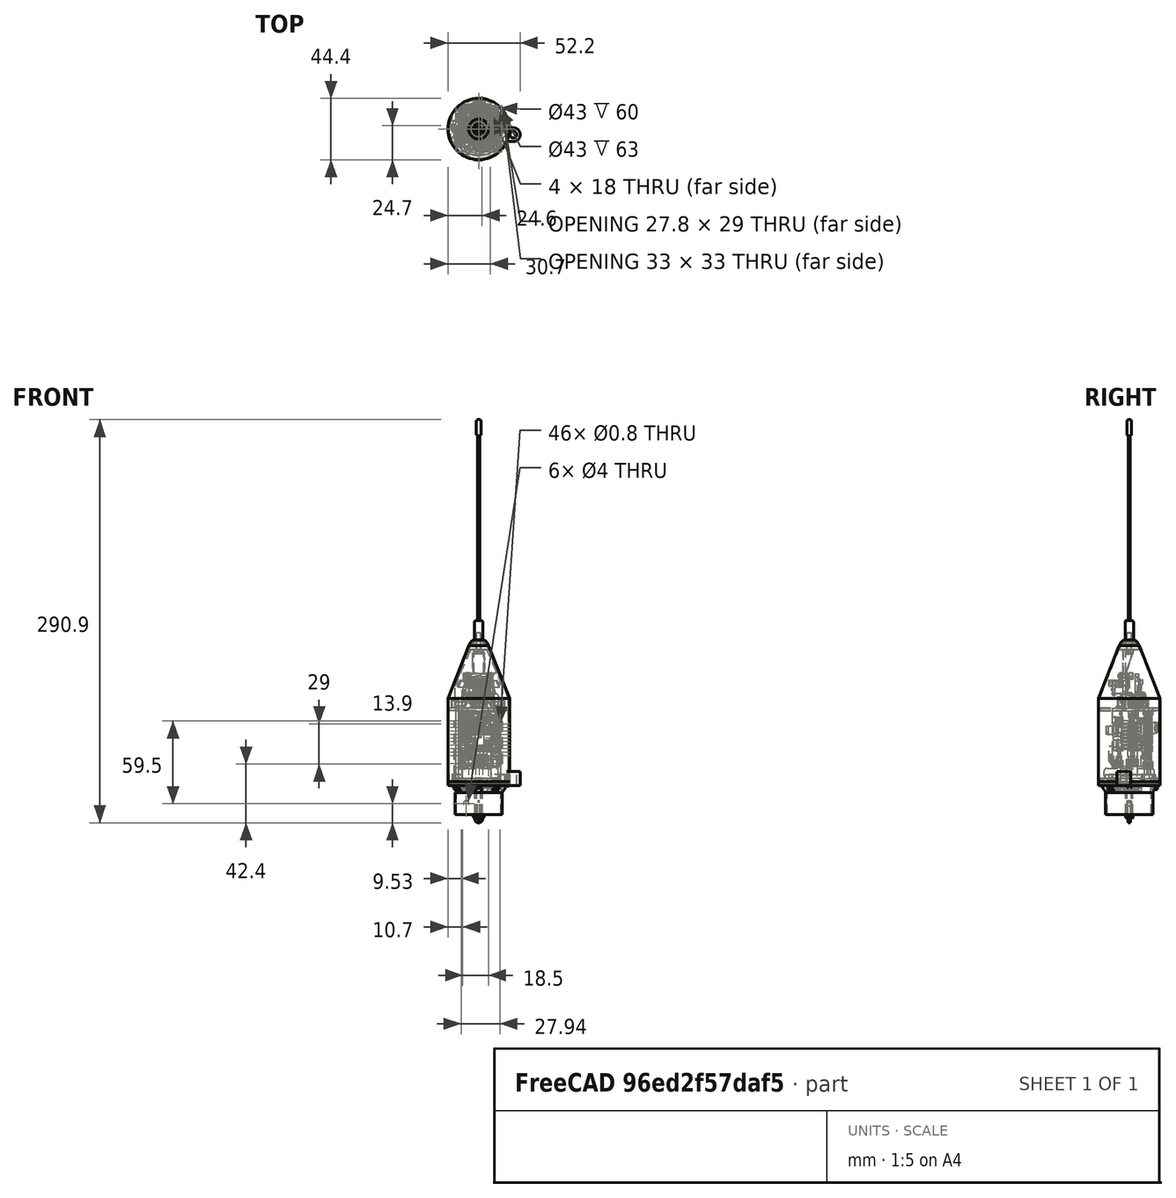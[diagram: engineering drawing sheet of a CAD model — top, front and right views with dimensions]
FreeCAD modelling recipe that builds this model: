
FCSTD DOCUMENT  (FreeCAD 0.18R4 (GitTag))
Label: fli3d structure v4.2
License: All rights reserved
LicenseURL: http://en.wikipedia.org/wiki/All_rights_reserved
objects: Part::Feature×223, Part::Cylinder×216, Part::Box×145, Part::Cut×97, Part::Compound×93, Part::Chamfer×44, Part::MultiFuse×30, Part::Prism×23, Part::Cone×9, Part::Fillet×7, Part::MultiCommon×7, Mesh::Feature×4, Part::Sphere×2, Part::Torus×1, App::Part×1
note: 897 computed .brp shape members not serialized (recipe doc carries the construction recipe); baked Part::Feature solids carry a one-line shape summary decoded from their .brp

FEATURE [Part::Cylinder] Cylinder
  Angle = 360
  AttacherType = Attacher::AttachEngine3D
  Height = 16
  Radius = 17
FEATURE [Part::Cylinder] Cylinder001  label="cut-out screw"
  Angle = 360
  AttacherType = Attacher::AttachEngine3D
  Height = 10
  Placement = pos=(0,0,1) rot=(0,0,1;0rad)
  Radius = 0.9
FEATURE [Part::Cylinder] Cylinder002
  Angle = 360
  AttacherType = Attacher::AttachEngine3D
  Height = 10
  Placement = pos=(0,0,-1) rot=(0,0,1;0rad)
  Radius = 0.9
FEATURE [Part::Torus] Torus
  Angle1 = -180
  Angle2 = 180
  Angle3 = 360
  AttacherType = Attacher::AttachEngine3D
  Placement = pos=(0,0,-3) rot=(1,0,0;1.5708rad)
  Radius1 = 2
  Radius2 = 0.9
FEATURE [Part::Compound] Compound  label="Eye screw"
  Links = -> [Torus,Cylinder002]
  Placement = pos=(0,0,1) rot=(0,0,1;0rad)
FEATURE [Part::Cylinder] Cylinder003
  Angle = 360
  AttacherType = Attacher::AttachEngine3D
  Height = 60
  Radius = 22.2
FEATURE [Part::Cylinder] Cylinder004
  Angle = 360
  AttacherType = Attacher::AttachEngine3D
  Height = 60
  Radius = 21.5
FEATURE [Part::Cut] Cut002
  Base = -> Cylinder003
  Placement = pos=(0,0,25) rot=(0,0,1;0rad)
  Tool = -> Cylinder004
FEATURE [Part::Cone] Cone001  label="Cone004"
  Angle = 360
  AttacherType = Attacher::AttachEngine3D
  Height = 41
  Placement = pos=(0,0,75) rot=(0,0,1;0rad)
  Radius1 = 22.2
  Radius2 = 6
FEATURE [Part::Cone] Cone002  label="Cone001"
  Angle = 360
  AttacherType = Attacher::AttachEngine3D
  Height = 41
  Placement = pos=(0,0,75) rot=(0,0,1;0rad)
  Radius1 = 21.5
  Radius2 = 5.3
FEATURE [Part::Cut] Cut003  label="compound"
  Base = -> Cone001
  Placement = pos=(0,0,10) rot=(0,0,1;0rad)
  Tool = -> Cone002
FEATURE [Part::Cylinder] Cylinder005
  Angle = 360
  AttacherType = Attacher::AttachEngine3D
  Height = 10
  Placement = pos=(0.5,26,66) rot=(1,0,0;1.5708rad)
  Radius = 2.75
FEATURE [Part::Cut] Cut004  label="cylindrical section"
  Base = -> Cut002
  Tool = -> Cylinder005
FEATURE [Part::Cylinder] Cylinder006
  Angle = 360
  AttacherType = Attacher::AttachEngine3D
  Height = 14
  Placement = pos=(0,0,150) rot=(0,0,1;0rad)
  Radius = 3
FEATURE [Part::Cylinder] Cylinder007
  Angle = 360
  AttacherType = Attacher::AttachEngine3D
  Height = 133
  Placement = pos=(0,0,164) rot=(0,0,1;0rad)
  Radius = 0.75
FEATURE [Part::Cylinder] Cylinder008
  Angle = 360
  AttacherType = Attacher::AttachEngine3D
  Height = 11.5
  Placement = pos=(0,0,297.5) rot=(0,0,1;0rad)
  Radius = 1.65
FEATURE [Part::Cylinder] Cylinder009
  Angle = 360
  AttacherType = Attacher::AttachEngine3D
  Height = 5
  Placement = pos=(0,0,150) rot=(0,0,1;0rad)
  Radius = 1.5
FEATURE [Part::Fillet] Fillet
  Base = -> Cylinder006
  Edges = 1 edges r=1: [Edge1]
FEATURE [Part::Cut] Cut005
  Base = -> Fillet
  Tool = -> Cylinder009
FEATURE [Part::Fillet] Fillet001
  Base = -> Cylinder008
  Edges = 2 edges r=1: [Edge1,Edge3]
FEATURE [Part::Compound] Compound003  label="433 MHz antenna"
  Links = -> [Cylinder007,Cut005,Fillet001]
  Placement = pos=(0,0,-23) rot=(0,0,1;0rad)
FEATURE [Part::Cylinder] Cylinder010
  Angle = 360
  AttacherType = Attacher::AttachEngine3D
  Height = 10
  Placement = pos=(0,0,118) rot=(0,0,1;0rad)
  Radius = 1.7
FEATURE [Part::Cylinder] Cylinder012
  Angle = 360
  AttacherType = Attacher::AttachEngine3D
  Height = 12
  Placement = pos=(0,0,-20) rot=(0,0,1;0rad)
  Radius = 1.5
FEATURE [Part::Cylinder] Cylinder013
  Angle = 360
  AttacherType = Attacher::AttachEngine3D
  Height = 3
  Placement = pos=(0,0,-23) rot=(0,0,1;0rad)
  Radius = 2.7
FEATURE [Part::Prism] Prism
  AttacherType = Attacher::AttachEngine3D
  Circumradius = 1.4
  Height = 2
  Placement = pos=(0,0,-23) rot=(0,0,1;0rad)
  Polygon = 6
FEATURE [Part::Cut] Cut008
  Base = -> Cylinder013
  Tool = -> Prism
FEATURE [Part::Compound] Compound005  label="M3x12 hex"
  Links = -> [Cylinder012,Cut008]
  Placement = pos=(0,0,140) rot=(0,0,1;0rad)
FEATURE [Part::Cylinder] Cylinder031
  Angle = 360
  AttacherType = Attacher::AttachEngine3D
  Height = 8
  Placement = pos=(0,0,-20) rot=(0,0,1;0rad)
  Radius = 1.25
FEATURE [Part::Cylinder] Cylinder032
  Angle = 360
  AttacherType = Attacher::AttachEngine3D
  Height = 2.5
  Placement = pos=(0,0,-22.5) rot=(0,0,1;0rad)
  Radius = 2.34
FEATURE [Part::Prism] Prism004
  AttacherType = Attacher::AttachEngine3D
  Circumradius = 1
  Height = 1.1
  Placement = pos=(0,0,-23) rot=(0,0,1;0rad)
  Polygon = 6
FEATURE [Part::Cut] Cut024
  Base = -> Cylinder032
  Tool = -> Prism004
FEATURE [Part::Compound] Compound013  label="M2.5x8 hex003"
  Links = -> [Cylinder031,Cut024]
  Placement = pos=(3,1,81) rot=(0,1,0;1.5708rad)
FEATURE [Part::Cylinder] Cylinder033
  Angle = 360
  AttacherType = Attacher::AttachEngine3D
  Height = 8
  Placement = pos=(0,0,-20) rot=(0,0,1;0rad)
  Radius = 1.25
FEATURE [Part::Cylinder] Cylinder034
  Angle = 360
  AttacherType = Attacher::AttachEngine3D
  Height = 2.5
  Placement = pos=(0,0,-22.5) rot=(0,0,1;0rad)
  Radius = 2.34
FEATURE [Part::Prism] Prism005
  AttacherType = Attacher::AttachEngine3D
  Circumradius = 1
  Height = 1.1
  Placement = pos=(0,0,-23) rot=(0,0,1;0rad)
  Polygon = 6
FEATURE [Part::Cut] Cut025
  Base = -> Cylinder034
  Tool = -> Prism005
FEATURE [Part::Compound] Compound014  label="M2.5x8 hex004"
  Links = -> [Cylinder033,Cut025]
  Placement = pos=(-4,8,81) rot=(0,-1,0;1.5708rad)
FEATURE [Part::Feature] Part__Feature183  label="pcb"
  shape: bbox 20.5 x 16 x 1.5 mm, 92 faces (baked)
FEATURE [Part::Feature] Part__Feature184  label="pcb001"
  shape: bbox 5.2 x 4.498 x 1 mm, 6 faces (baked)
FEATURE [Part::Feature] Part__Feature185  label="pcb002"
  shape: bbox 4.542 x 2.102 x 1.5 mm, 6 faces (baked)
FEATURE [Part::Feature] Part__Feature186  label="pcb003"
  shape: bbox 1.036 x 2.536 x 1 mm, 6 faces (baked)
FEATURE [Part::Feature] Part__Feature187  label="pcb004"
  shape: bbox 0.9209 x 2 x 1 mm, 6 faces (baked)
FEATURE [Part::Feature] Part__Feature188  label="pcb005"
  shape: bbox 1 x 2 x 1 mm, 6 faces (baked)
FEATURE [Part::Feature] Part__Feature189  label="pcb006"
  shape: bbox 1.036 x 2.536 x 1 mm, 6 faces (baked)
FEATURE [Part::Feature] Part__Feature190  label="pcb007"
  shape: bbox 1 x 2 x 1 mm, 6 faces (baked)
FEATURE [Part::Feature] Part__Feature191  label="pcb008"
  shape: bbox 2 x 1 x 1 mm, 6 faces (baked)
FEATURE [Part::Feature] Part__Feature192  label="pcb009"
  shape: bbox 1.036 x 2.536 x 1 mm, 6 faces (baked)
FEATURE [Part::Feature] Part__Feature193  label="pcb010"
  shape: bbox 1.036 x 2.536 x 1 mm, 6 faces (baked)
FEATURE [Part::Feature] Part__Feature194  label="pcb011"
  shape: bbox 0.9209 x 2 x 1 mm, 6 faces (baked)
FEATURE [Part::Feature] Part__Feature195  label="pcb012"
  shape: bbox 1.036 x 2.536 x 1 mm, 6 faces (baked)
FEATURE [Part::Feature] Part__Feature196  label="pcb013"
  shape: bbox 1.036 x 2.536 x 1 mm, 6 faces (baked)
FEATURE [Part::Feature] Part__Feature197  label="pcb014"
  shape: bbox 2.769 x 1.403 x 1 mm, 6 faces (baked)
FEATURE [Part::Feature] Part__Feature198  label="pcb015"
  shape: bbox 1.5 x 1.5 x 1.5 mm, 4 faces (baked)
FEATURE [Part::Feature] Part__Feature199  label="pcb016"
  shape: bbox 1.5 x 1.5 x 1.5 mm, 4 faces (baked)
FEATURE [Part::Feature] Part__Feature200  label="pcb017"
  shape: bbox 1.5 x 1.5 x 1.5 mm, 7 faces (baked)
FEATURE [Part::Feature] Part__Feature201  label="pcb018"
  shape: bbox 1.5 x 1.5 x 1.5 mm, 4 faces (baked)
FEATURE [Part::Feature] Part__Feature202  label="pcb019"
  shape: bbox 3.5 x 3.5 x 1.5 mm, 4 faces (baked)
FEATURE [Part::Feature] Part__Feature203  label="pcb020"
  shape: bbox 1.5 x 1.5 x 1.5 mm, 4 faces (baked)
FEATURE [Part::Feature] Part__Feature204  label="pcb021"
  shape: bbox 1.5 x 1.5 x 1.5 mm, 4 faces (baked)
FEATURE [Part::Feature] Part__Feature205  label="pcb022"
  shape: bbox 1.5 x 1.5 x 1.5 mm, 4 faces (baked)
FEATURE [Part::Feature] Part__Feature206  label="pcb023"
  shape: bbox 1.5 x 1.5 x 1.5 mm, 4 faces (baked)
FEATURE [Part::Feature] Part__Feature207  label="pcb024"
  shape: bbox 3.5 x 3.5 x 1.5 mm, 4 faces (baked)
FEATURE [Part::Feature] Part__Feature208  label="pcb025"
  shape: bbox 0.9 x 0.9 x 0.5 mm, 14 faces (baked)
FEATURE [Part::Feature] Part__Feature209  label="pcb026"
  shape: bbox 2.8 x 2.123 x 0.5 mm, 26 faces (baked)
FEATURE [Part::Feature] Part__Feature210  label="pcb027"
  shape: bbox 2.123 x 2.8 x 0.5 mm, 26 faces (baked)
FEATURE [Part::Feature] Part__Feature211  label="pcb028"
  shape: bbox 0.9 x 0.9 x 0.5 mm, 11 faces (baked)
FEATURE [Part::Feature] Part__Feature212  label="pin"
  Placement = pos=(-9,-7,-3) rot=(0,0,-1;1.5708rad)
  shape: bbox 0.64 x 7.5 x 7.3 mm, 18 faces (baked)
FEATURE [Part::Feature] Part__Feature213  label="pin header"
  Placement = pos=(-9,-7,-3) rot=(0,0,-1;1.5708rad)
  shape: bbox 2.54 x 2.54 x 2.54 mm, 22 faces (baked)
FEATURE [Part::Feature] Part__Feature214  label="pin001"
  Placement = pos=(-6.46,-7,-3) rot=(0,0,-1;1.5708rad)
  shape: bbox 0.64 x 7.5 x 7.3 mm, 18 faces (baked)
FEATURE [Part::Feature] Part__Feature215  label="pin002"
  Placement = pos=(-3.92,-7,-3) rot=(0,0,-1;1.5708rad)
  shape: bbox 0.64 x 7.5 x 7.3 mm, 18 faces (baked)
FEATURE [Part::Feature] Part__Feature216  label="pin003"
  Placement = pos=(-1.38,-7,-3) rot=(0,0,-1;1.5708rad)
  shape: bbox 0.64 x 7.5 x 7.3 mm, 18 faces (baked)
FEATURE [Part::Feature] Part__Feature217  label="pin004"
  Placement = pos=(1.16,-7,-3) rot=(0,0,-1;1.5708rad)
  shape: bbox 0.64 x 7.5 x 7.3 mm, 18 faces (baked)
FEATURE [Part::Feature] Part__Feature218  label="pin005"
  Placement = pos=(3.7,-7,-3) rot=(0,0,-1;1.5708rad)
  shape: bbox 0.64 x 7.5 x 7.3 mm, 18 faces (baked)
FEATURE [Part::Feature] Part__Feature219  label="pin006"
  Placement = pos=(6.24,-7,-3) rot=(0,0,-1;1.5708rad)
  shape: bbox 0.64 x 7.5 x 7.3 mm, 18 faces (baked)
FEATURE [Part::Feature] Part__Feature220  label="pin007"
  Placement = pos=(-9,-7,-3) rot=(0,0,-1;1.5708rad)
  shape: bbox 0.64 x 7.5 x 7.3 mm, 18 faces (baked)
FEATURE [Part::Feature] Part__Feature221  label="pin008"
  Placement = pos=(8.78,-7,-3) rot=(0,0,-1;1.5708rad)
  shape: bbox 0.64 x 7.5 x 7.3 mm, 18 faces (baked)
FEATURE [Part::Feature] Part__Feature222  label="pin header001"
  Placement = pos=(-6.46,-7,-3) rot=(0,0,-1;1.5708rad)
  shape: bbox 2.54 x 2.54 x 2.54 mm, 22 faces (baked)
FEATURE [Part::Feature] Part__Feature223  label="pin header002"
  Placement = pos=(-3.92,-7,-3) rot=(0,0,-1;1.5708rad)
  shape: bbox 2.54 x 2.54 x 2.54 mm, 22 faces (baked)
FEATURE [Part::Feature] Part__Feature224  label="pin header003"
  Placement = pos=(-1.38,-7,-3) rot=(0,0,-1;1.5708rad)
  shape: bbox 2.54 x 2.54 x 2.54 mm, 22 faces (baked)
FEATURE [Part::Feature] Part__Feature225  label="pin header004"
  Placement = pos=(1.16,-7,-3) rot=(0,0,-1;1.5708rad)
  shape: bbox 2.54 x 2.54 x 2.54 mm, 22 faces (baked)
FEATURE [Part::Feature] Part__Feature226  label="pin header005"
  Placement = pos=(3.7,-7,-3) rot=(0,0,-1;1.5708rad)
  shape: bbox 2.54 x 2.54 x 2.54 mm, 22 faces (baked)
FEATURE [Part::Feature] Part__Feature227  label="pin header006"
  Placement = pos=(6.24,-7,-3) rot=(0,0,-1;1.5708rad)
  shape: bbox 2.54 x 2.54 x 2.54 mm, 22 faces (baked)
FEATURE [Part::Feature] Part__Feature228  label="pin header007"
  Placement = pos=(8.78,-7,-3) rot=(0,0,-1;1.5708rad)
  shape: bbox 2.54 x 2.54 x 2.54 mm, 22 faces (baked)
FEATURE [Part::Compound] Compound019  label="MPU6050"
  Links = -> [Part__Feature183,Part__Feature227,Part__Feature226,Part__Feature184,Part__Feature185,Part__Feature186,Part__Feature187,Part__Feature188,Part__Feature189,Part__Feature190,Part__Feature191,Part__Feature192,Part__Feature193,Part__Feature194,Part__Feature195,Part__Feature196,Part__Feature197,Part__Feature198,Part__Feature199,Part__Feature200,Part__Feature201,Part__Feature202,Part__Feature203,+23 more]
  Placement = pos=(0,-1,95) rot=(0,0.707762,0.706451;3.14159rad)
FEATURE [Part::Feature] Part__Feature250  label="Compound"
  shape: bbox 0.64 x 7.3 x 7.5 mm, 18 faces (baked)
FEATURE [Part::Feature] Part__Feature251  label="Compound028"
  shape: bbox 0.9 x 0.55 x 1.7 mm, 36 faces (baked)
FEATURE [Part::Feature] Part__Feature252  label="Compound047"
  shape: bbox 0.9 x 0.55 x 1.7 mm, 36 faces (baked)
FEATURE [Part::Feature] Part__Feature253  label="Compound030"
  shape: bbox 1.7 x 0.9 x 0.9 mm, 34 faces (baked)
FEATURE [Part::Feature] Part__Feature254  label="Compound031"
  shape: bbox 0.64 x 7.3 x 7.5 mm, 18 faces (baked)
FEATURE [Part::Feature] Part__Feature255  label="Compound048"
  shape: bbox 0.9 x 0.55 x 1.7 mm, 36 faces (baked)
FEATURE [Part::Feature] Part__Feature256  label="Compound049"
  shape: bbox 0.64 x 7.3 x 7.5 mm, 18 faces (baked)
FEATURE [Part::Feature] Part__Feature257  label="Compound050"
  shape: bbox 2.518 x 0.974 x 2.018 mm, 265 faces (baked)
FEATURE [Part::Feature] Part__Feature258  label="Compound051"
  shape: bbox 0.9 x 0.9 x 1.7 mm, 34 faces (baked)
FEATURE [Part::Feature] Part__Feature259  label="Compound052"
  shape: bbox 0.9 x 0.55 x 1.7 mm, 36 faces (baked)
FEATURE [Part::Feature] Part__Feature260  label="Compound053"
  shape: bbox 0.64 x 7.3 x 7.5 mm, 18 faces (baked)
FEATURE [Part::Feature] Part__Feature261  label="Compound054"
  shape: bbox 0.64 x 7.3 x 7.5 mm, 18 faces (baked)
FEATURE [Part::Feature] Part__Feature262  label="Compound055"
  shape: bbox 15 x 1.57 x 11 mm, 14 faces (baked)
FEATURE [Part::Feature] Part__Feature263  label="Compound056"
  shape: bbox 0.64 x 7.3 x 7.5 mm, 18 faces (baked)
FEATURE [Part::Feature] Part__Feature264  label="Compound057"
  shape: bbox 2.54 x 2.799 x 2.54 mm, 22 faces, 0 solids (baked)
FEATURE [Part::Feature] Part__Feature265  label="Compound058"
  shape: bbox 2.54 x 2.799 x 2.54 mm, 23 faces, 0 solids (baked)
FEATURE [Part::Feature] Part__Feature266  label="Compound059"
  shape: bbox 2.54 x 2.799 x 2.54 mm, 23 faces, 0 solids (baked)
FEATURE [Part::Feature] Part__Feature267  label="Compound060"
  shape: bbox 2.54 x 2.799 x 2.54 mm, 22 faces, 0 solids (baked)
FEATURE [Part::Feature] Part__Feature268  label="Compound061"
  shape: bbox 2.54 x 2.799 x 2.54 mm, 22 faces, 0 solids (baked)
FEATURE [Part::Feature] Part__Feature269  label="Compound062"
  shape: bbox 2.54 x 2.799 x 2.54 mm, 22 faces, 0 solids (baked)
FEATURE [Part::Compound] Compound021  label="BMP280"
  Links = -> [Part__Feature250,Part__Feature268,Part__Feature262,Part__Feature269,Part__Feature255,Part__Feature258,Part__Feature266,Part__Feature261,Part__Feature259,Part__Feature265,Part__Feature254,Part__Feature257,Part__Feature263,Part__Feature252,Part__Feature267,Part__Feature264,Part__Feature260,Part__Feature256,Part__Feature251,Part__Feature253]
  Placement = pos=(3.5,-34.7,88.5) rot=(0,0,1;3.14159rad)
FEATURE [Part::Feature] Part__Feature270  label="XH2.54 4pin connector"
  Placement = pos=(-2.2,9.9,86) rot=(0,1,0;3.14159rad)
  shape: bbox 12.35 x 5.726 x 7.751 mm, 251 faces (baked)
FEATURE [Part::Feature] Part__Feature271  label="XH2.54 4pin connector001"
  Placement = pos=(-2.3,2.4,86) rot=(0,1,0;3.14159rad)
  shape: bbox 12.35 x 5.726 x 7.751 mm, 251 faces (baked)
FEATURE [Part::Feature] Part__Feature272  label="XH2.54 4pin connector 002"
  Placement = pos=(-2.2,-7.3,86) rot=(0,1,0;3.14159rad)
  shape: bbox 12.35 x 5.726 x 7.751 mm, 251 faces (baked)
FEATURE [Part::Feature] Part__Feature273  label="Compound002"
  shape: bbox 7.3 x 0.64 x 7.5 mm, 18 faces (baked)
FEATURE [Part::Feature] Part__Feature274  label="Compound063"
  shape: bbox 2.54 x 2.54 x 2.54 mm, 22 faces (baked)
FEATURE [Part::Feature] Part__Feature275  label="Compound064"
  shape: bbox 7.3 x 0.64 x 7.5 mm, 18 faces (baked)
FEATURE [Part::Feature] Part__Feature276  label="Compound065"
  shape: bbox 2.54 x 2.54 x 2.54 mm, 22 faces (baked)
FEATURE [Part::Feature] Part__Feature277  label="Compound066"
  shape: bbox 2.54 x 2.54 x 2.54 mm, 22 faces (baked)
FEATURE [Part::Feature] Part__Feature278  label="Compound067"
  shape: bbox 7.3 x 0.64 x 7.5 mm, 18 faces (baked)
FEATURE [Part::Feature] Part__Feature279  label="Compound068"
  shape: bbox 7.3 x 0.64 x 7.5 mm, 18 faces (baked)
FEATURE [Part::Feature] Part__Feature280  label="Compound069"
  shape: bbox 2.54 x 2.54 x 2.54 mm, 22 faces (baked)
FEATURE [Part::Feature] Part__Feature281  label="Compound070"
  shape: bbox 1 x 3 x 4 mm, 6 faces (baked)
FEATURE [Part::Feature] Part__Feature282  label="Compound071"
  shape: bbox 1 x 2 x 2 mm, 4 faces (baked)
FEATURE [Part::Feature] Part__Feature283  label="Compound072"
  shape: bbox 0.5 x 1.2 x 0.8 mm, 6 faces (baked)
FEATURE [Part::Feature] Part__Feature284  label="Compound073"
  shape: bbox 1 x 16 x 12 mm, 7 faces (baked)
FEATURE [Part::Feature] Part__Feature285  label="Compound074"
  shape: bbox 2 x 9.231 x 3.231 mm, 18 faces (baked)
FEATURE [Part::Feature] Part__Feature286  label="Compound075"
  shape: bbox 0.3 x 9.5 x 3.5 mm, 10 faces (baked)
FEATURE [Part::Feature] Part__Feature287  label="Compound076"
  shape: bbox 0.5 x 1.2 x 0.8 mm, 6 faces (baked)
FEATURE [Part::Feature] Part__Feature288  label="Compound077"
  shape: bbox 0.5 x 0.8 x 1.2 mm, 6 faces (baked)
FEATURE [Part::Feature] Part__Feature289  label="Compound078"
  shape: bbox 0.5 x 0.8 x 1.2 mm, 6 faces (baked)
FEATURE [Part::Feature] Part__Feature290  label="Compound079"
  shape: bbox 0.5 x 1.2 x 0.8 mm, 6 faces (baked)
FEATURE [Part::Feature] Part__Feature291  label="Compound080"
  shape: bbox 0.5 x 0.8 x 1.2 mm, 6 faces (baked)
FEATURE [Part::Feature] Part__Feature292  label="Compound081"
  shape: bbox 0.5 x 0.8 x 1.2 mm, 6 faces (baked)
FEATURE [Part::Feature] Part__Feature293  label="Compound082"
  shape: bbox 0.5 x 0.8 x 1.2 mm, 6 faces (baked)
FEATURE [Part::Compound] Compound025  label="WL102-341"
  Links = -> [Part__Feature273,Part__Feature286,Part__Feature291,Part__Feature282,Part__Feature274,Part__Feature288,Part__Feature293,Part__Feature284,Part__Feature283,Part__Feature292,Part__Feature277,Part__Feature276,Part__Feature285,Part__Feature290,Part__Feature281,Part__Feature287,Part__Feature289,Part__Feature280,Part__Feature279,Part__Feature278,Part__Feature275]
  Placement = pos=(8.5,6.5,99) rot=(0,0,1;1.5708rad)
FEATURE [Part::Cylinder] Cylinder044
  Angle = 360
  AttacherType = Attacher::AttachEngine3D
  Height = 3
  Placement = pos=(0,0,123) rot=(0,0,1;0rad)
  Radius = 8
FEATURE [Part::Cut] Cut038  label="conical section"
  Base = -> Cut003
  Tool = -> Cylinder044
FEATURE [Part::Cylinder] Cylinder045
  Angle = 360
  AttacherType = Attacher::AttachEngine3D
  Height = 4
  Placement = pos=(0,0,123) rot=(0,0,1;0rad)
  Radius = 9
FEATURE [Part::Sphere] Sphere
  Angle1 = 19
  Angle2 = 90
  Angle3 = 360
  AttacherType = Attacher::AttachEngine3D
  Placement = pos=(0,0,120.5) rot=(0,0,1;0rad)
  Radius = 7.6
FEATURE [Part::MultiCommon] Common002
  Shapes = -> [Cylinder045,Sphere]
FEATURE [Part::Cylinder] Cylinder046
  Angle = 360
  AttacherType = Attacher::AttachEngine3D
  Height = 3.1
  Placement = pos=(0,0,123) rot=(0,0,1;0rad)
  Radius = 4.3
FEATURE [Part::MultiFuse] Fusion006  label="uitsparing"
  Shapes = -> [Cylinder010,Cylinder046]
FEATURE [Part::Cut] Cut039  label="top"
  Base = -> Common002
  Tool = -> Fusion006
FEATURE [Part::Compound] Compound029  label="Structure (external)"
  Links = -> [Cut004,Cut038,Cut039]
FEATURE [Part::Cylinder] Cylinder053
  Angle = 360
  AttacherType = Attacher::AttachEngine3D
  Height = 8
  Placement = pos=(0,0,-20) rot=(0,0,1;0rad)
  Radius = 1.25
FEATURE [Part::Cylinder] Cylinder054
  Angle = 360
  AttacherType = Attacher::AttachEngine3D
  Height = 2.5
  Placement = pos=(0,0,-22.5) rot=(0,0,1;0rad)
  Radius = 2.34
FEATURE [Part::Prism] Prism009
  AttacherType = Attacher::AttachEngine3D
  Circumradius = 1
  Height = 1.1
  Placement = pos=(0,0,-23) rot=(0,0,1;0rad)
  Polygon = 6
FEATURE [Part::Cut] Cut044
  Base = -> Cylinder054
  Tool = -> Prism009
FEATURE [Part::Compound] Compound034  label="M2.5x8 hex005"
  Links = -> [Cylinder053,Cut044]
  Placement = pos=(-8,-20,101) rot=(1,0,0;1.5708rad)
FEATURE [Part::Cylinder] Cylinder055
  Angle = 360
  AttacherType = Attacher::AttachEngine3D
  Height = 8
  Placement = pos=(0,0,-20) rot=(0,0,1;0rad)
  Radius = 1.25
FEATURE [Part::Cylinder] Cylinder056
  Angle = 360
  AttacherType = Attacher::AttachEngine3D
  Height = 2.5
  Placement = pos=(0,0,-22.5) rot=(0,0,1;0rad)
  Radius = 2.34
FEATURE [Part::Prism] Prism010
  AttacherType = Attacher::AttachEngine3D
  Circumradius = 1
  Height = 1.1
  Placement = pos=(0,0,-23) rot=(0,0,1;0rad)
  Polygon = 6
FEATURE [Part::Cut] Cut045
  Base = -> Cylinder056
  Tool = -> Prism010
FEATURE [Part::Compound] Compound035  label="M2.5x8 hex006"
  Links = -> [Cylinder055,Cut045]
  Placement = pos=(8,-20,101) rot=(1,0,0;1.5708rad)
FEATURE [Part::Cylinder] Cylinder057
  Angle = 360
  AttacherType = Attacher::AttachEngine3D
  Height = 6
  Placement = pos=(0,0,-20) rot=(0,0,1;0rad)
  Radius = 1.25
FEATURE [Part::Cylinder] Cylinder058
  Angle = 360
  AttacherType = Attacher::AttachEngine3D
  Height = 2.5
  Placement = pos=(0,0,-22.5) rot=(0,0,1;0rad)
  Radius = 2.34
FEATURE [Part::Prism] Prism011
  AttacherType = Attacher::AttachEngine3D
  Circumradius = 1
  Height = 1.1
  Placement = pos=(0,0,-23) rot=(0,0,1;0rad)
  Polygon = 6
FEATURE [Part::Cut] Cut046
  Base = -> Cylinder058
  Tool = -> Prism011
FEATURE [Part::Compound] Compound036  label="M2.5x6 hex007"
  Links = -> [Cylinder057,Cut046]
  Placement = pos=(5.1,8,96) rot=(-1,0,0;1.5708rad)
FEATURE [Part::Cylinder] Cylinder059
  Angle = 360
  AttacherType = Attacher::AttachEngine3D
  Height = 6
  Placement = pos=(0,0,-20) rot=(0,0,1;0rad)
  Radius = 1.25
FEATURE [Part::Cylinder] Cylinder060
  Angle = 360
  AttacherType = Attacher::AttachEngine3D
  Height = 2.5
  Placement = pos=(0,0,-22.5) rot=(0,0,1;0rad)
  Radius = 2.34
FEATURE [Part::Prism] Prism012
  AttacherType = Attacher::AttachEngine3D
  Circumradius = 1
  Height = 1.1
  Placement = pos=(0,0,-23) rot=(0,0,1;0rad)
  Polygon = 6
FEATURE [Part::Cut] Cut047
  Base = -> Cylinder060
  Tool = -> Prism012
FEATURE [Part::Compound] Compound037  label="M2.5x6 hex008"
  Links = -> [Cylinder059,Cut047]
  Placement = pos=(-5.8,8,96) rot=(-1,0,0;1.5708rad)
FEATURE [Part::Feature] Part__Feature294  label="134N3P"
  Placement = pos=(-13,4.5,10) rot=(0,0,-1;1.5708rad)
  shape: bbox 26.49 x 17.15 x 5.666 mm, 1241 faces (baked)
FEATURE [Part::Box] Box051  label="connector access"
  AttacherType = Attacher::AttachEngine3D
  Height = 7
  Length = 12
  Placement = pos=(-6,-22,17) rot=(0,0,1;0rad)
  Width = 10
FEATURE [Part::Box] Box052  label="pcb cutout"
  AttacherType = Attacher::AttachEngine3D
  Height = 4
  Length = 18
  Placement = pos=(-9,-12.5,21) rot=(0,0,1;0rad)
  Width = 23
FEATURE [Part::Box] Box053  label="cutout wires"
  AttacherType = Attacher::AttachEngine3D
  Height = 3
  Length = 18
  Placement = pos=(-9,6.5,18) rot=(0,0,1;0rad)
  Width = 4
FEATURE [Part::Box] Box055  label="cutout components"
  AttacherType = Attacher::AttachEngine3D
  Height = 3.5
  Length = 14
  Placement = pos=(-7,-12.5,18) rot=(0,0,1;0rad)
  Width = 23
FEATURE [Part::MultiFuse] Fusion014  label="cutout 134N3P"
  Placement = pos=(0,0,-1) rot=(0,0,-1;1.5708rad)
  Shapes = -> [Box051,Box052,Box053,Box055]
FEATURE [Part::Cylinder] Cylinder065
  Angle = 360
  AttacherType = Attacher::AttachEngine3D
  Height = 6
  Placement = pos=(0,0,-20) rot=(0,0,1;0rad)
  Radius = 1.25
FEATURE [Part::Cylinder] Cylinder066
  Angle = 360
  AttacherType = Attacher::AttachEngine3D
  Height = 2.5
  Placement = pos=(0,0,-23) rot=(0,0,1;0rad)
  Radius = 2.34
FEATURE [Part::Prism] Prism013
  AttacherType = Attacher::AttachEngine3D
  Circumradius = 1.1
  Height = 1.1
  Placement = pos=(0,0,-23) rot=(0,0,1;0rad)
  Polygon = 6
FEATURE [Part::Cut] Cut059
  Base = -> Cylinder066
  Placement = pos=(0,0,0.5) rot=(0,0,1;0rad)
  Tool = -> Prism013
FEATURE [Part::Compound] Compound040  label="M2.5x6 hex011"
  Links = -> [Cylinder065,Cut059]
  Placement = pos=(-15,-10,5) rot=(1,0,0;3.14159rad)
FEATURE [Part::Cylinder] Cylinder067
  Angle = 360
  AttacherType = Attacher::AttachEngine3D
  Height = 6
  Placement = pos=(0,0,-20) rot=(0,0,1;0rad)
  Radius = 1.25
FEATURE [Part::Cylinder] Cylinder068
  Angle = 360
  AttacherType = Attacher::AttachEngine3D
  Height = 2.5
  Placement = pos=(0,0,-23) rot=(0,0,1;0rad)
  Radius = 2.34
FEATURE [Part::Prism] Prism014
  AttacherType = Attacher::AttachEngine3D
  Circumradius = 1.1
  Height = 1.1
  Placement = pos=(0,0,-23) rot=(0,0,1;0rad)
  Polygon = 6
FEATURE [Part::Cut] Cut060
  Base = -> Cylinder068
  Placement = pos=(0,0,0.5) rot=(0,0,1;0rad)
  Tool = -> Prism014
FEATURE [Part::Compound] Compound041  label="M2.5x6 hex012"
  Links = -> [Cylinder067,Cut060]
  Placement = pos=(12,-13,5) rot=(1,0,0;3.14159rad)
FEATURE [Part::Cylinder] Cylinder069
  Angle = 360
  AttacherType = Attacher::AttachEngine3D
  Height = 6
  Placement = pos=(0,0,-20) rot=(0,0,1;0rad)
  Radius = 1.25
FEATURE [Part::Cylinder] Cylinder070
  Angle = 360
  AttacherType = Attacher::AttachEngine3D
  Height = 2.5
  Placement = pos=(0,0,-23) rot=(0,0,1;0rad)
  Radius = 2.34
FEATURE [Part::Prism] Prism015
  AttacherType = Attacher::AttachEngine3D
  Circumradius = 1.1
  Height = 1.1
  Placement = pos=(0,0,-23) rot=(0,0,1;0rad)
  Polygon = 6
FEATURE [Part::Cut] Cut061
  Base = -> Cylinder070
  Placement = pos=(0,0,0.5) rot=(0,0,1;0rad)
  Tool = -> Prism015
FEATURE [Part::Compound] Compound042  label="M2.5x6 hex013"
  Links = -> [Cylinder069,Cut061]
  Placement = pos=(0,18,5) rot=(1,0,0;3.14159rad)
FEATURE [Part::Prism] Prism016
  AttacherType = Attacher::AttachEngine3D
  Circumradius = 3
  Height = 6
  Placement = pos=(0,0,-2) rot=(0,0,1;0rad)
  Polygon = 6
FEATURE [Part::Cylinder] Cylinder071
  Angle = 360
  AttacherType = Attacher::AttachEngine3D
  Height = 5
  Placement = pos=(0,0,1.4) rot=(0,0,1;0rad)
  Radius = 1.4
FEATURE [Part::MultiFuse] Fusion016  label="Screwnut"
  Placement = pos=(-15,-10,18) rot=(0,0,1;0rad)
  Shapes = -> [Prism016,Cylinder071]
FEATURE [Part::Prism] Prism017
  AttacherType = Attacher::AttachEngine3D
  Circumradius = 3
  Height = 6
  Placement = pos=(0,0,-2) rot=(0,0,1;0rad)
  Polygon = 6
FEATURE [Part::Cylinder] Cylinder072
  Angle = 360
  AttacherType = Attacher::AttachEngine3D
  Height = 5
  Placement = pos=(0,0,1.4) rot=(0,0,1;0rad)
  Radius = 1.4
FEATURE [Part::MultiFuse] Fusion017  label="Screwnut001"
  Placement = pos=(12,-13,18) rot=(0,0,1;0rad)
  Shapes = -> [Prism017,Cylinder072]
FEATURE [Part::Prism] Prism018
  AttacherType = Attacher::AttachEngine3D
  Circumradius = 3
  Height = 6
  Placement = pos=(0,0,-2) rot=(0,0,1;0rad)
  Polygon = 6
FEATURE [Part::Cylinder] Cylinder073
  Angle = 360
  AttacherType = Attacher::AttachEngine3D
  Height = 5
  Placement = pos=(0,0,1.4) rot=(0,0,1;0rad)
  Radius = 1.4
FEATURE [Part::MultiFuse] Fusion018  label="Screwnut002"
  Placement = pos=(0,18,18) rot=(0,0,1;0rad)
  Shapes = -> [Prism018,Cylinder073]
FEATURE [Part::Box] Box058  label="wire cutout"
  AttacherType = Attacher::AttachEngine3D
  Height = 10
  Length = 4
  Placement = pos=(-2,-19,15) rot=(0,0,1;0rad)
  Width = 3
FEATURE [Part::Prism] Prism019  label="M2.5 nut011"
  AttacherType = Attacher::AttachEngine3D
  Circumradius = 2.72
  Height = 2
  Placement = pos=(12,-13,19) rot=(0,0,1;0rad)
  Polygon = 6
FEATURE [Part::Prism] Prism020  label="M2.5 nut012"
  AttacherType = Attacher::AttachEngine3D
  Circumradius = 2.72
  Height = 2
  Placement = pos=(0,18,19) rot=(0,0,1;0rad)
  Polygon = 6
FEATURE [Part::Prism] Prism021  label="M2.5 nut013"
  AttacherType = Attacher::AttachEngine3D
  Circumradius = 2.72
  Height = 2
  Placement = pos=(-15,-10,19) rot=(0,0,1;0rad)
  Polygon = 6
FEATURE [Part::Prism] Prism022  label="M2.5 nut"
  AttacherType = Attacher::AttachEngine3D
  Circumradius = 2.72
  Height = 2
  Placement = pos=(9,8,81) rot=(0,1,0;1.5708rad)
  Polygon = 6
FEATURE [Part::Prism] Prism023  label="M2.5 nut001"
  AttacherType = Attacher::AttachEngine3D
  Circumradius = 2.72
  Height = 2
  Placement = pos=(-11.5,1,81) rot=(0,1,0;1.5708rad)
  Polygon = 6
FEATURE [Part::Prism] Prism024  label="M2.5 nut002"
  AttacherType = Attacher::AttachEngine3D
  Circumradius = 2.72
  Height = 2
  Placement = pos=(-6,-6,96) rot=(1,0,0;1.5708rad)
  Polygon = 6
FEATURE [Part::Prism] Prism025  label="M2.5 nut003"
  AttacherType = Attacher::AttachEngine3D
  Circumradius = 2.72
  Height = 2
  Placement = pos=(8,-5,101) rot=(1,0,0;1.5708rad)
  Polygon = 6
FEATURE [Part::Prism] Prism026  label="M2.5 nut004"
  AttacherType = Attacher::AttachEngine3D
  Circumradius = 2.72
  Height = 2
  Placement = pos=(5,-6,96) rot=(1,0,0;1.5708rad)
  Polygon = 6
FEATURE [Part::Prism] Prism027  label="M2.5 nut005"
  AttacherType = Attacher::AttachEngine3D
  Circumradius = 2.72
  Height = 2
  Placement = pos=(-8,-5,101) rot=(1,0,0;1.5708rad)
  Polygon = 6
FEATURE [Part::Cone] Cone  label="Cone003"
  Angle = 360
  AttacherType = Attacher::AttachEngine3D
  Height = 8
  Placement = pos=(0,0,17) rot=(0,0,1;0rad)
  Radius1 = 17
  Radius2 = 22
FEATURE [Part::Compound] Compound112  label="Content (top)"
  Links = -> [Compound019,Compound025,Compound014,Compound021,Compound013,Compound005,Compound003,Part__Feature270,Part__Feature271,Part__Feature272,Compound036,Compound034,Compound037,Compound035,Prism025,Prism027,Prism024,Prism023,Prism026,Prism022]
FEATURE [Part::Cylinder] Cylinder223
  Angle = 360
  AttacherType = Attacher::AttachEngine3D
  Height = 18
  Radius = 16
FEATURE [Part::Cut] Cut  label="Cut118"
  Base = -> Cylinder
  Placement = pos=(0,0,1) rot=(0,0,1;0rad)
  Tool = -> Cylinder223
FEATURE [Part::Box] Box189  label="Cube176"
  AttacherType = Attacher::AttachEngine3D
  Height = 16
  Length = 3
  Placement = pos=(-1.5,-16.5,1) rot=(0,0,1;0rad)
  Width = 33
FEATURE [Part::Cylinder] Cylinder224
  Angle = 360
  AttacherType = Attacher::AttachEngine3D
  Height = 16
  Placement = pos=(0,0,1) rot=(0,0,1;0rad)
  Radius = 3
FEATURE [Part::Box] Box190  label="Cube177"
  AttacherType = Attacher::AttachEngine3D
  Height = 42
  Length = 1.9
  Placement = pos=(-14.4,11,34) rot=(0,0,1;0rad)
  Width = 5
FEATURE [Part::Box] Box191  label="Cube178"
  AttacherType = Attacher::AttachEngine3D
  Height = 8
  Length = 1.8
  Placement = pos=(-16.4,-4,76) rot=(0,0,1;0rad)
  Width = 10
FEATURE [Part::Box] Box194  label="Cube181"
  AttacherType = Attacher::AttachEngine3D
  Height = 42
  Length = 1
  Placement = pos=(13,11,34) rot=(0,0,1;0rad)
  Width = 5
FEATURE [Part::Box] Box195  label="Cube182"
  AttacherType = Attacher::AttachEngine3D
  Height = 2
  Length = 4
  Placement = pos=(-2,-18,23) rot=(0,0,1;0rad)
  Width = 2
FEATURE [Part::Cylinder] Cylinder227
  Angle = 360
  AttacherType = Attacher::AttachEngine3D
  Height = 2
  Placement = pos=(12,-13,23) rot=(0,0,1;0rad)
  Radius = 1.4
FEATURE [Part::Box] Box196  label="Cube183"
  AttacherType = Attacher::AttachEngine3D
  Height = 2
  Length = 4
  Placement = pos=(6.5,-9,23) rot=(0,0,1;0rad)
  Width = 18
FEATURE [Part::Cylinder] Cylinder228  label="Cylinder240"
  Angle = 360
  AttacherType = Attacher::AttachEngine3D
  Height = 62
  Placement = pos=(0,0,23) rot=(0,0,1;0rad)
  Radius = 21
FEATURE [Part::Cylinder] Cylinder229  label="Cylinder237"
  Angle = 360
  AttacherType = Attacher::AttachEngine3D
  Height = 10
  Placement = pos=(-20,1,81) rot=(0,1,0;1.5708rad)
  Radius = 1.5
FEATURE [Part::Cut] Cut137  label="Top attachment001"
  Base = -> Box191
  Tool = -> Cylinder229
FEATURE [Part::Fillet] Fillet024  label="Top attachment"
  Base = -> Cut137
  Edges = 2 edges r=2: [Edge8,Edge9]
FEATURE [Part::Box] Box197  label="side plate cut-out006"
  AttacherType = Attacher::AttachEngine3D
  Height = 7.1
  Length = 2
  Placement = pos=(-16.4,9,23) rot=(0,0,1;0rad)
  Width = 7
FEATURE [Part::Cylinder] Cylinder231
  Angle = 360
  AttacherType = Attacher::AttachEngine3D
  Height = 5
  Placement = pos=(0,18,25) rot=(0,0,1;0rad)
  Radius = 2.5
FEATURE [Part::Box] Box201  label="side plate cut-out008"
  AttacherType = Attacher::AttachEngine3D
  Height = 12
  Length = 2
  Placement = pos=(-16.4,-16,23) rot=(0,0,1;0rad)
  Width = 10
FEATURE [Part::Box] Box202  label="Cube186"
  AttacherType = Attacher::AttachEngine3D
  Height = 9
  Length = 2
  Placement = pos=(14,10.5,76) rot=(0,0,1;0rad)
  Width = 5.5
FEATURE [Part::Cylinder] Cylinder233
  Angle = 360
  AttacherType = Attacher::AttachEngine3D
  Height = 2
  Placement = pos=(-15,-10,23) rot=(0,0,1;0rad)
  Radius = 1.4
FEATURE [Part::Box] Box203  label="Cube187"
  AttacherType = Attacher::AttachEngine3D
  Height = 62
  Length = 2
  Placement = pos=(14,-2,23) rot=(0,0,1;0rad)
  Width = 18
FEATURE [Part::Cylinder] Cylinder234
  Angle = 360
  AttacherType = Attacher::AttachEngine3D
  Height = 5
  Placement = pos=(-15,-10,25) rot=(0,0,1;0rad)
  Radius = 2.5
FEATURE [Part::Cylinder] Cylinder235
  Angle = 360
  AttacherType = Attacher::AttachEngine3D
  Height = 2
  Placement = pos=(0,0,23) rot=(0,0,1;0rad)
  Radius = 22
FEATURE [Part::MultiFuse] Fusion060  label="Acceptable volume (centre)004"
  Shapes = -> [Cylinder235,Cylinder228]
FEATURE [Part::Cylinder] Cylinder236  label="Cylinder229"
  Angle = 360
  AttacherType = Attacher::AttachEngine3D
  Height = 5
  Placement = pos=(0,0,25) rot=(0,0,-1;0rad)
  Radius = 21
FEATURE [Part::Cylinder] Cylinder237  label="Cylinder232"
  Angle = 360
  AttacherType = Attacher::AttachEngine3D
  Height = 10
  Placement = pos=(10,7.75,81) rot=(0,1,0;1.5708rad)
  Radius = 1.5
FEATURE [Part::Box] Box204  label="cut-out ESP32-CAM"
  AttacherType = Attacher::AttachEngine3D
  Height = 41
  Length = 27.6
  Placement = pos=(-13.5,13,35) rot=(0,0,1;0rad)
  Width = 1.9
FEATURE [Part::Cylinder] Cylinder238
  Angle = 360
  AttacherType = Attacher::AttachEngine3D
  Height = 2
  Placement = pos=(0,18,23) rot=(0,0,1;0rad)
  Radius = 1.4
FEATURE [Part::Cylinder] Cylinder239
  Angle = 360
  AttacherType = Attacher::AttachEngine3D
  Height = 2
  Placement = pos=(0,0,23) rot=(0,0,1;0rad)
  Radius = 22
FEATURE [Part::Cylinder] Cylinder240  label="Cylinder236"
  Angle = 360
  AttacherType = Attacher::AttachEngine3D
  Height = 5
  Placement = pos=(0,0,25) rot=(0,0,-1;0rad)
  Radius = 19
FEATURE [Part::Cut] Cut131  label="ring002"
  Base = -> Cylinder236
  Tool = -> Cylinder240
FEATURE [Part::Cylinder] Cylinder241
  Angle = 360
  AttacherType = Attacher::AttachEngine3D
  Height = 5
  Placement = pos=(12,-13,25) rot=(0,0,1;0rad)
  Radius = 2.5
FEATURE [Part::Box] Box208  label="side plate base"
  AttacherType = Attacher::AttachEngine3D
  Height = 53
  Length = 2
  Placement = pos=(-16.4,-12,23) rot=(0,0,1;0rad)
  Width = 28
FEATURE [Part::Box] Box209  label="Cube192"
  AttacherType = Attacher::AttachEngine3D
  Height = 7.5
  Length = 6
  Placement = pos=(9,-19,27) rot=(0,0,1;0rad)
  Width = 8
FEATURE [Part::Box] Box211  label="Cube194"
  AttacherType = Attacher::AttachEngine3D
  Height = 7.5
  Length = 21
  Placement = pos=(-12,-21,27) rot=(0,0,1;0rad)
  Width = 42
FEATURE [Part::MultiFuse] Fusion055  label="ring cut-outs001"
  Shapes = -> [Box209,Cylinder231,Cylinder234,Cylinder241,Box211]
FEATURE [Part::Cut] Cut133  label="Base ring001"
  Base = -> Cut131
  Tool = -> Fusion055
FEATURE [Part::Box] Box212  label="cutout ESP32-CAM004"
  AttacherType = Attacher::AttachEngine3D
  Height = 41
  Length = 27.6
  Placement = pos=(-13.5,13,35) rot=(0,0,1;0rad)
  Width = 1.9
FEATURE [Part::Cut] Cut129  label="ESP32cam clamping001"
  Base = -> Box194
  Tool = -> Box212
FEATURE [Part::Box] Box213  label="Cube195"
  AttacherType = Attacher::AttachEngine3D
  Height = 7.1
  Length = 2
  Placement = pos=(14,10,23) rot=(0,0,1;0rad)
  Width = 6
FEATURE [Part::Box] Box216  label="Cube198"
  AttacherType = Attacher::AttachEngine3D
  Height = 5
  Length = 5
  Placement = pos=(-14,4.5,36) rot=(0,0,1;0rad)
  Width = 3
FEATURE [Part::Chamfer] Chamfer033  label="Chamfer045"
  Base = -> Box216
  Edges = 1 edges: [Edge7 r1=2 r2=4]
  Placement = pos=(-0.4,-1,0) rot=(0,0,1;0rad)
FEATURE [Part::Box] Box219  label="Cube201"
  AttacherType = Attacher::AttachEngine3D
  Height = 5
  Length = 5
  Width = 3
FEATURE [Part::Chamfer] Chamfer035  label="Chamfer047"
  Base = -> Box219
  Edges = 1 edges: [Edge5 r1=2 r2=4]
  Placement = pos=(-14.4,-1.3,36) rot=(0,0,1;0rad)
FEATURE [Part::Box] Box220  label="Cube202"
  AttacherType = Attacher::AttachEngine3D
  Height = 2
  Length = 2.2
  Placement = pos=(13.9,-2.1,23) rot=(0,0,1;0rad)
  Width = 12.2
FEATURE [Part::Box] Box221  label="Cube203"
  AttacherType = Attacher::AttachEngine3D
  Height = 2
  Length = 2.2
  Placement = pos=(-16.5,-6.1,23) rot=(0,0,1;0rad)
  Width = 15.2
FEATURE [Part::Box] Box222  label="Cube204"
  AttacherType = Attacher::AttachEngine3D
  Height = 5
  Length = 5
  Placement = pos=(-14,4.5,36) rot=(0,0,1;0rad)
  Width = 3
FEATURE [Part::Chamfer] Chamfer032  label="Chamfer044"
  Base = -> Box222
  Edges = 1 edges: [Edge7 r1=2 r2=4]
  Placement = pos=(-0.4,-1,35) rot=(0,0,1;0rad)
FEATURE [Part::Feature] Part__Feature327  label="Pin Header 4 x 1 TH 2.54mm Pitch v033"
  Placement = pos=(4.72,-2.66216,2.20216) rot=(0.57735,0.57735,0.57735;4.18879rad)
  shape: bbox 0.635 x 11.43 x 0.635 mm, 14 faces (baked)
FEATURE [Mesh::Feature] __54_pin_header008  label="2.54_pin_header008"
  Placement = pos=(8.5,27.2,-0.8) rot=(0,0,1;0rad)
FEATURE [Part::Box] Box224  label="wifi antenna001"
  AttacherType = Attacher::AttachEngine3D
  Height = 40
  Length = 1
  Placement = pos=(-17.5,-6,29) rot=(0,0,1;0rad)
  Width = 12
FEATURE [Part::Feature] Part__Feature328  label="Pin Header 4 x 1 TH 2.54mm Pitch v034"
  Placement = pos=(14.89,-2.66216,25.2022) rot=(0.57735,0.57735,0.57735;4.18879rad)
  shape: bbox 0.635 x 11.43 x 0.635 mm, 14 faces (baked)
FEATURE [Part::Feature] Part__Feature329  label="Pin Header 4 x 1 TH 2.54mm Pitch v035"
  Placement = pos=(4.72,-2.66216,2.20216) rot=(0.57735,0.57735,0.57735;4.18879rad)
  shape: bbox 0.635 x 11.43 x 0.635 mm, 14 faces (baked)
FEATURE [Part::Feature] Part__Feature330  label="Pin Header 4 x 1 TH 2.54mm Pitch v036"
  Placement = pos=(14.89,-2.66216,25.2022) rot=(0.57735,0.57735,0.57735;4.18879rad)
  shape: bbox 0.635 x 11.43 x 0.635 mm, 14 faces (baked)
FEATURE [Part::Feature] Part__Feature331  label="Pin Header 4 x 1 TH 2.54mm Pitch v037"
  Placement = pos=(4.72,-2.66216,2.20216) rot=(0.57735,0.57735,0.57735;4.18879rad)
  shape: bbox 0.635 x 11.43 x 0.635 mm, 14 faces (baked)
FEATURE [Part::Feature] Part__Feature332  label="Pin Header 4 x 1 TH 2.54mm Pitch v038"
  Placement = pos=(14.883,-2.66216,2.20216) rot=(0.57735,0.57735,0.57735;4.18879rad)
  shape: bbox 0.635 x 11.43 x 0.635 mm, 14 faces (baked)
FEATURE [Part::Feature] Part__Feature333  label="Pin Header 4 x 1 TH 2.54mm Pitch v039"
  Placement = pos=(14.89,-2.66216,25.2022) rot=(0.57735,0.57735,0.57735;4.18879rad)
  shape: bbox 0.635 x 11.43 x 0.635 mm, 14 faces (baked)
FEATURE [Part::Feature] Part__Feature334  label="Pin Header 4 x 1 TH 2.54mm Pitch v040"
  Placement = pos=(14.89,-2.66216,25.2022) rot=(0.57735,0.57735,0.57735;4.18879rad)
  shape: bbox 0.635 x 11.43 x 0.635 mm, 14 faces (baked)
FEATURE [Part::Feature] Part__Feature335  label="Pin Header 4 x 1 TH 2.54mm Pitch v041"
  Placement = pos=(4.72,-2.66216,2.20216) rot=(0.57735,0.57735,0.57735;4.18879rad)
  shape: bbox 0.635 x 11.43 x 0.635 mm, 14 faces (baked)
FEATURE [Part::Feature] Part__Feature336  label="Pin Header 4 x 1 TH 2.54mm Pitch v042"
  Placement = pos=(4.71,-2.66216,25.2022) rot=(-0.57735,-0.57735,-0.57735;2.0944rad)
  shape: bbox 0.635 x 11.43 x 0.635 mm, 14 faces (baked)
FEATURE [Part::Feature] Part__Feature337  label="Pin Header 4 x 1 TH 2.54mm Pitch v043"
  Placement = pos=(4.71,-2.66216,25.2022) rot=(-0.57735,-0.57735,-0.57735;2.0944rad)
  shape: bbox 0.635 x 11.43 x 0.635 mm, 14 faces (baked)
FEATURE [Part::Feature] Part__Feature338  label="Pin Header 4 x 1 TH 2.54mm Pitch v044"
  Placement = pos=(14.883,-2.66216,2.20216) rot=(0.57735,0.57735,0.57735;4.18879rad)
  shape: bbox 0.635 x 11.43 x 0.635 mm, 14 faces (baked)
FEATURE [Part::Feature] Part__Feature339  label="Pin Header 4 x 1 TH 2.54mm Pitch v045"
  Placement = pos=(14.883,-2.66216,2.20216) rot=(0.57735,0.57735,0.57735;4.18879rad)
  shape: bbox 0.635 x 11.43 x 0.635 mm, 14 faces (baked)
FEATURE [Part::Feature] Part__Feature340  label="Pin Header 4 x 1 TH 2.54mm Pitch v046"
  Placement = pos=(14.883,-2.66216,2.20216) rot=(0.57735,0.57735,0.57735;4.18879rad)
  shape: bbox 0.635 x 11.43 x 0.635 mm, 14 faces (baked)
FEATURE [Part::Feature] Part__Feature341  label="u005"
  Placement = pos=(30.5196,-1.14548,7.21031) rot=(1,0,0;3.14159rad)
  shape: bbox 1.8 x 0.165 x 0.4527 mm, 9 faces (baked)
FEATURE [Part::Feature] Part__Feature342  label="u006"
  Placement = pos=(30.5196,-1.14548,7.21031) rot=(1,0,0;3.14159rad)
  shape: bbox 0.5465 x 0.165 x 0.6 mm, 7 faces (baked)
FEATURE [Part::Feature] Part__Feature343  label="switch-3x4x2mm - 2 Pad v002"
  Placement = pos=(4,0.684989,21.7704) rot=(1,0,0;1.5708rad)
  shape: bbox 5.004 x 1.93 x 2.997 mm, 237 faces (baked)
FEATURE [Part::Feature] Part__Feature344  label="Pin Header 4 x 1 TH 2.54mm Pitch v047"
  Placement = pos=(4.71,-2.66216,25.2022) rot=(-0.57735,-0.57735,-0.57735;2.0944rad)
  shape: bbox 0.635 x 11.43 x 0.635 mm, 14 faces (baked)
FEATURE [Part::Feature] Part__Feature345  label="nano - reg001"
  Placement = pos=(4.45,-0.0046987,14.7657) rot=(-0.707107,0,0.707107;3.14159rad)
  shape: bbox 8.304 x 1.695 x 6.504 mm, 194 faces (baked)
FEATURE [Part::Feature] Part__Feature346  label="Pin Header 4 x 1 TH 2.54mm Pitch v048"
  Placement = pos=(4.71,-2.66216,25.2022) rot=(-0.57735,-0.57735,-0.57735;2.0944rad)
  shape: bbox 0.635 x 11.43 x 0.635 mm, 14 faces (baked)
FEATURE [Part::Compound] Compound121  label="pins001"
  Links = -> [Part__Feature344,Part__Feature340,Part__Feature332,Part__Feature337,Part__Feature334,Part__Feature346,Part__Feature339,Part__Feature330,Part__Feature328,Part__Feature338,Part__Feature335,Part__Feature336,Part__Feature329,Part__Feature327,Part__Feature331,Part__Feature333]
FEATURE [Part::Feature] Part__Feature347  label="u007"
  Placement = pos=(30.5196,-1.14548,7.21031) rot=(1,0,0;3.14159rad)
  shape: bbox 1.8 x 0.165 x 0.4527 mm, 9 faces (baked)
FEATURE [Part::Feature] Part__Feature348  label="u008"
  Placement = pos=(30.5196,-1.14548,7.21031) rot=(1,0,0;3.14159rad)
  shape: bbox 2.616 x 1.25 x 2.633 mm, 39 faces (baked)
FEATURE [Part::Feature] Part__Feature349  label="u009"
  Placement = pos=(30.5196,-1.14548,7.21031) rot=(1,0,0;3.14159rad)
  shape: bbox 0.5465 x 0.165 x 0.6 mm, 7 faces (baked)
FEATURE [Part::Feature] Part__Feature350  label="SOLID004"
  Placement = pos=(15.3712,-0.145481,22.8712) rot=(0.707107,0,-0.707107;3.14159rad)
  shape: bbox 19.24 x 3.435 x 18.07 mm, 845 faces (baked)
FEATURE [Part::Feature] Part__Feature351  label="capacitor-CAPM-TANTB-YL v004"
  Placement = pos=(11,0.104975,22.105) rot=(1,0,0;1.5708rad)
  shape: bbox 3.446 x 2.076 x 3.006 mm, 54 faces (baked)
FEATURE [Part::Feature] Part__Feature352  label="capacitor-CAPM-TANTB-YL v005"
  Placement = pos=(11,0.104975,22.105) rot=(1,0,0;1.5708rad)
  shape: bbox 1 x 1.13 x 2.2 mm, 18 faces (baked)
FEATURE [Part::Feature] Part__Feature353  label="capacitor-CAPM-TANTB-YL v006"
  Placement = pos=(11,0.104975,22.105) rot=(1,0,0;1.5708rad)
  shape: bbox 1 x 1.13 x 2.2 mm, 18 faces (baked)
FEATURE [Part::Feature] Part__Feature354  label="resistor-NTC-0402-T0.6 v021"
  Placement = pos=(10.2,0,12.3) rot=(0,1,0;1.5708rad)
  shape: bbox 0.6 x 0.55 x 1.1 mm, 42 faces (baked)
FEATURE [Part::Feature] Part__Feature355  label="Component009"
  Placement = pos=(4,-1.3e-14,7) rot=(0.57735,-0.57735,0.57735;2.0944rad)
  shape: bbox 1 x 1.05 x 0.4 mm, 14 faces (baked)
FEATURE [Part::Feature] Part__Feature356  label="Component5(Mirror)004"
  Placement = pos=(4,-1.2e-14,8.27) rot=(0.57735,0.57735,0.57735;4.18879rad)
  shape: bbox 1 x 1.05 x 0.4 mm, 14 faces (baked)
FEATURE [Part::Feature] Part__Feature357  label="icbody001"
  Placement = pos=(4,-1.3e-14,7) rot=(0.57735,-0.57735,0.57735;2.0944rad)
  shape: bbox 3.9 x 1.45 x 4.9 mm, 50 faces (baked)
FEATURE [Part::Feature] Part__Feature358  label="Component010"
  Placement = pos=(4,-1.5e-14,5.73) rot=(0.57735,-0.57735,0.57735;2.0944rad)
  shape: bbox 1 x 1.05 x 0.4 mm, 14 faces (baked)
FEATURE [Part::Feature] Part__Feature359  label="Component5(Mirror)005"
  Placement = pos=(4,-1.3e-14,7) rot=(0.57735,0.57735,0.57735;4.18879rad)
  shape: bbox 1 x 1.05 x 0.4 mm, 14 faces (baked)
FEATURE [Part::Feature] Part__Feature360  label="Component5(Mirror)006"
  Placement = pos=(4,-1.6e-14,4.46) rot=(0.57735,0.57735,0.57735;4.18879rad)
  shape: bbox 1 x 1.05 x 0.4 mm, 14 faces (baked)
FEATURE [Part::Feature] Part__Feature361  label="Component011"
  Placement = pos=(4,-1.6e-14,4.46) rot=(0.57735,-0.57735,0.57735;2.0944rad)
  shape: bbox 1 x 1.05 x 0.4 mm, 14 faces (baked)
FEATURE [Part::Feature] Part__Feature362  label="Component5(Mirror)007"
  Placement = pos=(4,-1.5e-14,5.73) rot=(0.57735,0.57735,0.57735;4.18879rad)
  shape: bbox 1 x 1.05 x 0.4 mm, 14 faces (baked)
FEATURE [Part::Feature] Part__Feature363  label="Fusion054"
  Placement = pos=(12,-5e-15,18) rot=(0.57735,-0.57735,0.57735;2.0944rad)
  shape: bbox 0.8 x 0.5 x 1.6 mm, 25 faces (baked)
FEATURE [Part::Feature] Part__Feature364  label="Fillet034"
  Placement = pos=(12,-5e-15,18) rot=(0.57735,-0.57735,0.57735;2.0944rad)
  shape: bbox 0.8 x 0.3 x 1.2 mm, 18 faces (baked)
FEATURE [Part::Feature] Part__Feature365  label="resistor-NTC-0402-T0.6 v022"
  Placement = pos=(12.2,0,15.8) rot=(0,1,0;1.5708rad)
  shape: bbox 0.6 x 0.55 x 1.1 mm, 42 faces (baked)
FEATURE [Part::Feature] Part__Feature366  label="Component012"
  Placement = pos=(4,-1.2e-14,8.27) rot=(0.57735,-0.57735,0.57735;2.0944rad)
  shape: bbox 1 x 1.05 x 0.4 mm, 14 faces (baked)
FEATURE [Part::Feature] Part__Feature367  label="smd-transistor-SOT23-3 v017"
  Placement = pos=(27,1.05803,23.942) rot=(-1,0,0;1.5708rad)
  shape: bbox 0.6498 x 0.8933 x 0.6 mm, 7 faces (baked)
FEATURE [Part::Feature] Part__Feature368  label="smd-transistor-SOT23-3 v018"
  Placement = pos=(27,1.05803,2.44197) rot=(-1,0,0;1.5708rad)
  shape: bbox 0.6498 x 0.8933 x 0.6 mm, 7 faces (baked)
FEATURE [Part::Feature] Part__Feature369  label="resistor-NTC-0402-T0.6 v023"
  Placement = pos=(25.5,0,24.5) rot=(0,0,1;0rad)
  shape: bbox 1.1 x 0.55 x 0.6 mm, 42 faces (baked)
FEATURE [Part::Feature] Part__Feature370  label="resistor-NTC-0402-T0.6 v024"
  Placement = pos=(28.5,0,24.5) rot=(0,0,1;0rad)
  shape: bbox 1.1 x 0.55 x 0.6 mm, 42 faces (baked)
FEATURE [Part::Feature] Part__Feature371  label="smd-transistor-SOT23-3 v019"
  Placement = pos=(27,1.05803,2.44197) rot=(-1,0,0;1.5708rad)
  shape: bbox 0.6498 x 0.8933 x 0.6 mm, 7 faces (baked)
FEATURE [Part::Feature] Part__Feature372  label="resistor-NTC-0402-T0.6 v025"
  Placement = pos=(32.5,0,24.5) rot=(0,0,1;0rad)
  shape: bbox 1.1 x 0.55 x 0.6 mm, 42 faces (baked)
FEATURE [Part::Feature] Part__Feature373  label="smd-transistor-SOT23-3 v020"
  Placement = pos=(27,1.05803,2.44197) rot=(-1,0,0;1.5708rad)
  shape: bbox 0.6498 x 0.8933 x 0.6 mm, 7 faces (baked)
FEATURE [Part::Feature] Part__Feature374  label="smd-transistor-SOT23-3 v021"
  Placement = pos=(27,1.05803,2.44197) rot=(-1,0,0;1.5708rad)
  shape: bbox 1.651 x 1.1 x 3 mm, 34 faces (baked)
FEATURE [Part::Feature] Part__Feature375  label="resistor-NTC-0402-T0.6 v026"
  Placement = pos=(4.5,0,10.6) rot=(0,1,0;3.14159rad)
  shape: bbox 1.1 x 0.55 x 0.6 mm, 42 faces (baked)
FEATURE [Part::Feature] Part__Feature376  label="smd-transistor-SOT23-3 v022"
  Placement = pos=(27,1.05803,23.942) rot=(-1,0,0;1.5708rad)
  shape: bbox 0.6498 x 0.8933 x 0.6 mm, 7 faces (baked)
FEATURE [Part::Feature] Part__Feature377  label="smd-transistor-SOT23-3 v023"
  Placement = pos=(27,1.05803,23.942) rot=(-1,0,0;1.5708rad)
  shape: bbox 0.6498 x 0.8933 x 0.6 mm, 7 faces (baked)
FEATURE [Part::Feature] Part__Feature378  label="resistor-NTC-0805-T1.3 v002"
  Placement = pos=(10.35,0,14.65) rot=(0,1,0;1.5708rad)
  shape: bbox 1.3 x 1.4 x 2.2 mm, 42 faces (baked)
FEATURE [Part::Feature] Part__Feature379  label="resistor-NTC-0402-T0.6 v027"
  Placement = pos=(11.2,0,5.97136) rot=(0,1,0;1.5708rad)
  shape: bbox 0.6 x 0.55 x 1.1 mm, 42 faces (baked)
FEATURE [Part::Feature] Part__Feature380  label="resistor-NTC-0402-T0.6 v028"
  Placement = pos=(17.7,1,4.3) rot=(0,1,0;1.5708rad)
  shape: bbox 0.6 x 0.55 x 1.1 mm, 42 faces (baked)
FEATURE [Part::Feature] Part__Feature381  label="resistor-NTC-0402-T0.6 v029"
  Placement = pos=(18.7,1,4.3) rot=(0,1,0;1.5708rad)
  shape: bbox 0.6 x 0.55 x 1.1 mm, 42 faces (baked)
FEATURE [Part::Feature] Part__Feature382  label="resistor-NTC-0402-T0.6 v030"
  Placement = pos=(21,1,5.2) rot=(0,0,1;0rad)
  shape: bbox 1.1 x 0.55 x 0.6 mm, 42 faces (baked)
FEATURE [Part::Feature] Part__Feature383  label="resistor-NTC-0402-T0.6 v031"
  Placement = pos=(29.3,1,24.3) rot=(0,-1,0;1.5708rad)
  shape: bbox 0.6 x 0.55 x 1.1 mm, 42 faces (baked)
FEATURE [Part::Feature] Part__Feature384  label="smd-transistor-SOT23-3 v024"
  Placement = pos=(27,1.05803,23.942) rot=(-1,0,0;1.5708rad)
  shape: bbox 1.651 x 1.1 x 3 mm, 34 faces (baked)
FEATURE [Part::Feature] Part__Feature385  label="resistor-NTC-0402-T0.6 v032"
  Placement = pos=(30.3,1,24.3) rot=(0,-1,0;1.5708rad)
  shape: bbox 0.6 x 0.55 x 1.1 mm, 42 faces (baked)
FEATURE [Part::Feature] Part__Feature386  label="resistor-NTC-0402-T0.6 v033"
  Placement = pos=(19.7,1,4.3) rot=(0,1,0;1.5708rad)
  shape: bbox 0.6 x 0.55 x 1.1 mm, 42 faces (baked)
FEATURE [Part::Feature] Part__Feature387  label="resistor-NTC-0402-T0.6 v034"
  Placement = pos=(20.7,1,4.3) rot=(0,1,0;1.5708rad)
  shape: bbox 0.6 x 0.55 x 1.1 mm, 42 faces (baked)
FEATURE [Part::Feature] Part__Feature388  label="resistor-NTC-0402-T0.6 v035"
  Placement = pos=(18,1,6.2) rot=(0,0,1;0rad)
  shape: bbox 1.1 x 0.55 x 0.6 mm, 42 faces (baked)
FEATURE [Part::Feature] Part__Feature389  label="resistor-NTC-0402-T0.6 v036"
  Placement = pos=(18,1,7.2) rot=(0,0,1;0rad)
  shape: bbox 1.1 x 0.55 x 0.6 mm, 42 faces (baked)
FEATURE [Part::Feature] Part__Feature390  label="capacitor-CAPC-0603-T0.9-BN v003"
  Placement = pos=(21,1,7) rot=(0,0,1;0rad)
  shape: bbox 1.7 x 0.9 x 0.9 mm, 42 faces (baked)
FEATURE [Part::Feature] Part__Feature391  label="LED SMD 5050 White v002"
  Placement = pos=(30,1.2963,2.10027) rot=(-1,0,0;1.5708rad)
  shape: bbox 5.4 x 1.62 x 5 mm, 76 faces (baked)
FEATURE [Part::Feature] Part__Feature392  label="resistor-NTC-0402-T0.6 v037"
  Placement = pos=(31,1,17) rot=(0,0,1;0rad)
  shape: bbox 1.1 x 0.55 x 0.6 mm, 42 faces (baked)
FEATURE [Part::Feature] Part__Feature393  label="smd-transistor-SOT23-3 v025"
  Placement = pos=(21.5739,1.05803,19.0158) rot=(-0.57735,0.57735,0.57735;2.0944rad)
  shape: bbox 0.6 x 0.8933 x 0.6498 mm, 7 faces (baked)
FEATURE [Part::Feature] Part__Feature394  label="smd-transistor-SOT23-3 v026"
  Placement = pos=(21.5739,1.05803,19.0158) rot=(-0.57735,0.57735,0.57735;2.0944rad)
  shape: bbox 0.6 x 0.8933 x 0.6498 mm, 7 faces (baked)
FEATURE [Part::Feature] Part__Feature395  label="connector smd usl00-20l_p0-4_l12-6_w2-75 v002"
  Placement = pos=(26.791,1,14.009) rot=(0,1,0;1.5708rad)
  shape: bbox 3.1 x 1 x 12.6 mm, 645 faces (baked)
FEATURE [Part::Feature] Part__Feature396  label="smd-transistor-SOT23-3 v027"
  Placement = pos=(21.5739,1.05803,19.0158) rot=(-0.57735,0.57735,0.57735;2.0944rad)
  shape: bbox 3 x 1.1 x 1.651 mm, 34 faces (baked)
FEATURE [Part::Feature] Part__Feature397  label="resistor-NTC-0402-T0.6 v038"
  Placement = pos=(18,1,14.2) rot=(0,0,1;0rad)
  shape: bbox 1.1 x 0.55 x 0.6 mm, 42 faces (baked)
FEATURE [Part::Feature] Part__Feature398  label="capacitor-CAPC-0603-T0.9-BN v004"
  Placement = pos=(22,1,21) rot=(0,0,1;0rad)
  shape: bbox 1.7 x 0.9 x 0.9 mm, 42 faces (baked)
FEATURE [Part::Feature] Part__Feature399  label="smd-transistor-SOT23-3 v028"
  Placement = pos=(21.5739,1.05803,10.0158) rot=(-0.57735,0.57735,0.57735;2.0944rad)
  shape: bbox 0.6 x 0.8933 x 0.6498 mm, 7 faces (baked)
FEATURE [Part::Feature] Part__Feature400  label="smd-transistor-SOT23-3 v029"
  Placement = pos=(21.5739,1.05803,10.0158) rot=(-0.57735,0.57735,0.57735;2.0944rad)
  shape: bbox 0.6 x 0.8933 x 0.6498 mm, 7 faces (baked)
FEATURE [Part::Feature] Part__Feature401  label="smd-transistor-SOT23-3 v030"
  Placement = pos=(21.5739,1.05803,10.0158) rot=(-0.57735,0.57735,0.57735;2.0944rad)
  shape: bbox 3 x 1.1 x 1.651 mm, 34 faces (baked)
FEATURE [Part::Feature] Part__Feature402  label="resistor-NTC-0402-T0.6 v039"
  Placement = pos=(21,1,6) rot=(0,0,1;0rad)
  shape: bbox 1.1 x 0.55 x 0.6 mm, 42 faces (baked)
FEATURE [Part::Feature] Part__Feature403  label="smd-transistor-SOT23-3 v031"
  Placement = pos=(21.5739,1.05803,19.0158) rot=(-0.57735,0.57735,0.57735;2.0944rad)
  shape: bbox 0.6 x 0.8933 x 0.6498 mm, 7 faces (baked)
FEATURE [Part::Feature] Part__Feature404  label="smd-transistor-SOT23-3 v032"
  Placement = pos=(21.5739,1.05803,10.0158) rot=(-0.57735,0.57735,0.57735;2.0944rad)
  shape: bbox 0.6 x 0.8933 x 0.6498 mm, 7 faces (baked)
FEATURE [Part::Feature] Part__Feature405  label="resistor-NTC-0402-T0.6 v040"
  Placement = pos=(18,1,13.2) rot=(0,0,1;0rad)
  shape: bbox 1.1 x 0.55 x 0.6 mm, 42 faces (baked)
FEATURE [Part::Feature] Part__Feature406  label="Micro SD-Card v010"
  Placement = pos=(7,2.64,12.5) rot=(0,0,1;0rad)
  shape: bbox 3.1 x 0.01 x 0.95 mm, 10 faces (baked)
FEATURE [Part::Feature] Part__Feature407  label="Micro SD-Card v011"
  Placement = pos=(7,2.64,12.5) rot=(0,0,1;0rad)
  shape: bbox 3.1 x 0.01 x 0.95 mm, 10 faces (baked)
FEATURE [Part::Feature] Part__Feature408  label="Micro SD-Card v012"
  Placement = pos=(7,2.64,12.5) rot=(0,0,1;0rad)
  shape: bbox 3.1 x 0.01 x 0.95 mm, 10 faces (baked)
FEATURE [Part::Feature] Part__Feature409  label="Micro SD-Card v013"
  Placement = pos=(7,2.64,12.5) rot=(0,0,1;0rad)
  shape: bbox 3.1 x 0.01 x 0.95 mm, 10 faces (baked)
FEATURE [Part::Feature] Part__Feature410  label="Micro SD-Card v014"
  Placement = pos=(7,2.64,12.5) rot=(0,0,1;0rad)
  shape: bbox 3.1 x 0.01 x 0.95 mm, 10 faces (baked)
FEATURE [Part::Feature] Part__Feature411  label="User Library-ov9655_ov9655_flex_reinf001"
  Placement = pos=(24.1466,3.31977,13.5126) rot=(0.57735,-0.57735,-0.57735;4.18879rad)
  shape: bbox 4.5 x 0.25 x 12.5 mm, 6 faces (baked)
FEATURE [Part::Feature] Part__Feature412  label="AMS1118"
  Placement = pos=(26.2661,1.87,19.328) rot=(0,0,1;0rad)
FEATURE [Part::Feature] Part__Feature413  label="User Library-ov9655_ov9655_flex_pcb001"
  Placement = pos=(24.1466,3.31977,13.5126) rot=(0.57735,-0.57735,-0.57735;4.18879rad)
  shape: bbox 21.5 x 0.12 x 12.5 mm, 20 faces (baked)
FEATURE [Part::Feature] Part__Feature414  label="sdreader001"
  Placement = pos=(15.4256,-0.2,14.568) rot=(-1,0,0;1.5708rad)
  shape: bbox 15 x 2.025 x 16 mm, 54 faces (baked)
FEATURE [Part::Feature] Part__Feature415  label="Micro SD-Card v015"
  Placement = pos=(7,2.64,12.5) rot=(0,0,1;0rad)
  shape: bbox 3.35 x 0.01 x 0.95 mm, 10 faces (baked)
FEATURE [Part::Feature] Part__Feature416  label="Micro SD-Card v016"
  Placement = pos=(7,2.64,12.5) rot=(0,0,1;0rad)
  shape: bbox 3.35 x 0.01 x 0.95 mm, 10 faces (baked)
FEATURE [Part::Feature] Part__Feature417  label="Micro SD-Card v017"
  Placement = pos=(7,2.64,12.5) rot=(0,0,1;0rad)
  shape: bbox 15 x 1 x 11.09 mm, 23 faces (baked)
FEATURE [Part::Feature] Part__Feature418  label="Micro SD-Card v018"
  Placement = pos=(7,2.64,12.5) rot=(0,0,1;0rad)
  shape: bbox 3.1 x 0.01 x 0.95 mm, 10 faces (baked)
FEATURE [Part::Feature] Part__Feature419  label="User Library-ov9655_ov9655_body001"
  Placement = pos=(24.1466,3.31977,13.5126) rot=(0.57735,-0.57735,-0.57735;4.18879rad)
  shape: bbox 8.847 x 6.041 x 8.847 mm, 59 faces (baked)
FEATURE [Part::Feature] Part__Feature420  label="User Library-ov9655_ov9655_lens001"
  Placement = pos=(24.1466,3.31977,13.5126) rot=(0.57735,-0.57735,-0.57735;4.18879rad)
  shape: bbox 2 x 1.43 x 2 mm, 3 faces (baked)
FEATURE [Part::Feature] Part__Feature421  label="SOLID005"
  shape: bbox 40 x 1 x 27 mm, 10 faces (baked)
FEATURE [Part::Cut] Cut143  label="PCB004"
  Base = -> Part__Feature421
  Tool = -> Compound121
FEATURE [Part::Feature] Part__Feature422  label="User Library-ov9655_ov9655_back_panel001"
  Placement = pos=(24.1466,3.31977,13.5126) rot=(0.57735,-0.57735,-0.57735;4.18879rad)
  shape: bbox 8.5 x 0.25 x 8.5 mm, 10 faces (baked)
FEATURE [Part::Compound] Compound122  label="ESP32-CAM001"
  Links = -> [Cut143,Part__Feature369,Part__Feature361,Part__Feature418,Part__Feature363,Part__Feature390,Part__Feature414,Part__Feature356,Part__Feature382,Part__Feature392,Part__Feature408,Part__Feature365,Part__Feature351,Part__Feature345,Part__Feature398,Part__Feature384,Part__Feature359,Part__Feature404,Part__Feature354,Part__Feature371,Part__Feature352,Part__Feature420,Part__Feature405,Part__Feature402,+56 more]
  Placement = pos=(-13,13,75) rot=(0,1,0;1.5708rad)
FEATURE [Part::Feature] Part__Feature423  label="SOLID006"
  Placement = pos=(0,0,0) rot=(-1,0,0;1.5708rad)
  shape: bbox 7.981 x 5.431 x 2.941 mm, 406 faces (baked)
FEATURE [App::Part] _73460003  label="micro USB002"
  Group = -> [Part__Feature423]
  Origin = -> Origin002
  Placement = pos=(2,16,-1.3) rot=(0,0,1;1.5708rad)
FEATURE [Part::Feature] Part__Feature424  label="GPS_res475"
  Placement = pos=(-13.49,1.3,-12.319) rot=(0,-1,0;1.5708rad)
  shape: bbox 1.02 x 0.6154 x 2.362 mm, 138 faces, 4 solids (baked)
FEATURE [Part::Feature] Part__Feature425  label="GPS_res476"
  Placement = pos=(-16.49,1.3,-12.319) rot=(0,-1,0;1.5708rad)
  shape: bbox 1.02 x 0.6154 x 2.362 mm, 138 faces, 4 solids (baked)
FEATURE [Part::Feature] Part__Feature426  label="GPS_battery001"
  Placement = pos=(-14.7943,1.29979,13.0331) rot=(-0.850961,-0.371393,-0.371393;1.73149rad)
  shape: bbox 5.675 x 1.701 x 5.675 mm, 36 faces (baked)
FEATURE [Part::Feature] Part__Feature427  label="GPS_res477"
  Placement = pos=(-11.4616,1.3,-12.319) rot=(0,1,0;1.5708rad)
  shape: bbox 1.02 x 0.6154 x 2.362 mm, 124 faces, 4 solids (baked)
FEATURE [Part::Feature] Part__Feature428  label="GPS_res478"
  Placement = pos=(-20.7044,1.68325,10.5205) rot=(0,0,1;0rad)
  shape: bbox 2.362 x 0.6154 x 1.02 mm, 124 faces, 4 solids (baked)
FEATURE [Part::Feature] Part__Feature429  label="GPS_res479"
  Placement = pos=(-11.2066,1.68325,10.5205) rot=(0,0,1;0rad)
  shape: bbox 2.362 x 0.6154 x 1.02 mm, 124 faces, 4 solids (baked)
FEATURE [Part::Feature] Part__Feature430  label="GPS_cap001"
  Placement = pos=(-1.008,1.35775,-12.1193) rot=(0,-1,0;1.5708rad)
  shape: bbox 1.226 x 0.955 x 3.329 mm, 56 faces (baked)
FEATURE [Part::Feature] Part__Feature431  label="GPS_led001"
  Placement = pos=(-15.9936,1.3,10.5305) rot=(0,0,1;0rad)
  shape: bbox 3.551 x 0.7528 x 1.711 mm, 57 faces, 2 solids (baked)
FEATURE [Part::Box] Box225  label="battery volume002"
  AttacherType = Attacher::AttachEngine3D
  Height = 7.5
  Length = 21
  Width = 36
FEATURE [Part::Fillet] Fillet028  label="Battery001"
  Base = -> Box225
  Edges = 12 edges r=2: [Edge1,Edge2,Edge3,Edge4,Edge5,Edge6,Edge7,Edge8,Edge9,Edge10,Edge11,Edge12]
  Placement = pos=(-12,-18,27) rot=(0,0,1;0rad)
FEATURE [Part::Box] Box226  label="Cube206"
  AttacherType = Attacher::AttachEngine3D
  Height = 1.5
  Length = 39
  Width = 31.4
FEATURE [Part::Chamfer] Chamfer047  label="Chamfer066"
  Base = -> Box226
  Edges = 2 edges r=2: [Edge5,Edge7]
FEATURE [Part::Box] Box227  label="Cube207"
  AttacherType = Attacher::AttachEngine3D
  Height = 1.5
  Length = 6.7
  Width = 2.8
FEATURE [Part::Fillet] Fillet029  label="Fillet035"
  Base = -> Box227
  Edges = 1 edges r=1.5: [Edge7]
FEATURE [Part::Box] Box228  label="Cube208"
  AttacherType = Attacher::AttachEngine3D
  Height = 1.5
  Length = 1.1
  Placement = pos=(0,10.5,0) rot=(0,0,1;0rad)
  Width = 11
FEATURE [Part::Chamfer] Chamfer048
  Base = -> Box228
  Edges = 2 edges r=1: [Edge5,Edge7]
FEATURE [Part::MultiFuse] Fusion061
  Shapes = -> [Chamfer048,Fillet029]
FEATURE [Part::Box] Box229  label="Antenna002"
  AttacherType = Attacher::AttachEngine3D
  Height = 0.9
  Length = 26
  Placement = pos=(13.1,7,-0.9) rot=(0,0,1;0rad)
  Width = 18.2
FEATURE [Part::Box] Box230  label="ESP033"
  AttacherType = Attacher::AttachEngine3D
  Height = 2.2
  Length = 17.6
  Placement = pos=(14.5,8,-3.2) rot=(0,0,1;0rad)
  Width = 15.8
FEATURE [Part::Cut] Cut160  label="PCB005"
  Base = -> Chamfer047
  Tool = -> Fusion061
FEATURE [Mesh::Feature] __54_pin_header009  label="2.54_pin_header009"
  Placement = pos=(8.5,1.7,-0.8) rot=(0,0,1;0rad)
FEATURE [Mesh::Feature] __54_pin_header010  label="2.54_pin_header010"
  Placement = pos=(21.2,1.7,-0.8) rot=(0,0,1;0rad)
FEATURE [Part::Box] Box231  label="Cube209"
  AttacherType = Attacher::AttachEngine3D
  Height = 1
  Length = 2
  Placement = pos=(2.3,1.6,-1.5) rot=(0,0,1;0rad)
  Width = 1.2
FEATURE [Part::Cylinder] Cylinder254
  Angle = 360
  AttacherType = Attacher::AttachEngine3D
  Height = 1.5
  Radius = 0.9
FEATURE [Part::Cylinder] Cylinder255
  Angle = 360
  AttacherType = Attacher::AttachEngine3D
  Height = 1.5
  Radius = 0.4
FEATURE [Part::Cylinder] Cylinder256
  Angle = 360
  AttacherType = Attacher::AttachEngine3D
  Height = 1.5
  Radius = 0.9
FEATURE [Part::Cut] Cut158
  Base = -> Cylinder256
  Tool = -> Cylinder255
FEATURE [Part::Box] Box232  label="Cube210"
  AttacherType = Attacher::AttachEngine3D
  Height = 2
  Length = 4.7
  Placement = pos=(1,2.8,-2) rot=(0,0,1;0rad)
  Width = 2.5
FEATURE [Part::Cylinder] Cylinder257
  Angle = 360
  AttacherType = Attacher::AttachEngine3D
  Height = 1.5
  Radius = 0.4
FEATURE [Part::Cylinder] Cylinder258
  Angle = 360
  AttacherType = Attacher::AttachEngine3D
  Height = 1.5
  Radius = 0.4
FEATURE [Part::Cylinder] Cylinder259
  Angle = 360
  AttacherType = Attacher::AttachEngine3D
  Height = 1.5
  Radius = 0.4
FEATURE [Part::Cylinder] Cylinder260
  Angle = 360
  AttacherType = Attacher::AttachEngine3D
  Height = 1.5
  Radius = 0.9
FEATURE [Part::Cylinder] Cylinder261
  Angle = 360
  AttacherType = Attacher::AttachEngine3D
  Height = 1.5
  Radius = 0.9
FEATURE [Part::Cylinder] Cylinder262
  Angle = 360
  AttacherType = Attacher::AttachEngine3D
  Height = 1.5
  Radius = 0.9
FEATURE [Part::Cut] Cut159
  Base = -> Cylinder262
  Placement = pos=(22.86,0,0) rot=(0,0,1;0rad)
  Tool = -> Cylinder258
FEATURE [Part::Cylinder] Cylinder263
  Angle = 360
  AttacherType = Attacher::AttachEngine3D
  Height = 1.5
  Radius = 0.4
FEATURE [Part::Cylinder] Cylinder264
  Angle = 360
  AttacherType = Attacher::AttachEngine3D
  Height = 1.5
  Radius = 0.4
FEATURE [Part::Cylinder] Cylinder265
  Angle = 360
  AttacherType = Attacher::AttachEngine3D
  Height = 1.5
  Radius = 0.9
FEATURE [Part::Cylinder] Cylinder266
  Angle = 360
  AttacherType = Attacher::AttachEngine3D
  Height = 1.5
  Radius = 0.9
FEATURE [Part::Cylinder] Cylinder267
  Angle = 360
  AttacherType = Attacher::AttachEngine3D
  Height = 1.5
  Radius = 0.4
FEATURE [Part::Cut] Cut149
  Base = -> Cylinder261
  Placement = pos=(15.24,0,0) rot=(0,0,1;0rad)
  Tool = -> Cylinder267
FEATURE [Part::Cylinder] Cylinder268
  Angle = 360
  AttacherType = Attacher::AttachEngine3D
  Height = 1.5
  Radius = 0.9
FEATURE [Part::Cylinder] Cylinder269
  Angle = 360
  AttacherType = Attacher::AttachEngine3D
  Height = 1.5
  Radius = 0.4
FEATURE [Part::Cut] Cut150
  Base = -> Cylinder268
  Placement = pos=(2.54,0,0) rot=(0,0,1;0rad)
  Tool = -> Cylinder269
FEATURE [Part::Cylinder] Cylinder270
  Angle = 360
  AttacherType = Attacher::AttachEngine3D
  Height = 1.5
  Radius = 0.4
FEATURE [Part::Cut] Cut162
  Base = -> Cylinder265
  Placement = pos=(20.32,0,0) rot=(0,0,1;0rad)
  Tool = -> Cylinder270
FEATURE [Part::Cylinder] Cylinder271
  Angle = 360
  AttacherType = Attacher::AttachEngine3D
  Height = 1.5
  Radius = 0.4
FEATURE [Part::Cut] Cut156
  Base = -> Cylinder266
  Placement = pos=(5.08,0,0) rot=(0,0,1;0rad)
  Tool = -> Cylinder271
FEATURE [Part::Cylinder] Cylinder272
  Angle = 360
  AttacherType = Attacher::AttachEngine3D
  Height = 1.5
  Radius = 0.4
FEATURE [Part::Cylinder] Cylinder273
  Angle = 360
  AttacherType = Attacher::AttachEngine3D
  Height = 1.5
  Radius = 0.4
FEATURE [Part::Cylinder] Cylinder274
  Angle = 360
  AttacherType = Attacher::AttachEngine3D
  Height = 1.5
  Radius = 0.9
FEATURE [Part::Cut] Cut161
  Base = -> Cylinder274
  Placement = pos=(10.16,0,0) rot=(0,0,1;0rad)
  Tool = -> Cylinder272
FEATURE [Part::Cylinder] Cylinder275
  Angle = 360
  AttacherType = Attacher::AttachEngine3D
  Height = 1.5
  Radius = 0.9
FEATURE [Part::Cut] Cut148
  Base = -> Cylinder275
  Placement = pos=(7.62,0,0) rot=(0,0,1;0rad)
  Tool = -> Cylinder257
FEATURE [Part::Cylinder] Cylinder276
  Angle = 360
  AttacherType = Attacher::AttachEngine3D
  Height = 1.5
  Radius = 0.9
FEATURE [Part::Cylinder] Cylinder277
  Angle = 360
  AttacherType = Attacher::AttachEngine3D
  Height = 1.5
  Radius = 0.4
FEATURE [Part::Cut] Cut155
  Base = -> Cylinder276
  Placement = pos=(17.78,0,0) rot=(0,0,1;0rad)
  Tool = -> Cylinder277
FEATURE [Part::Cylinder] Cylinder278
  Angle = 360
  AttacherType = Attacher::AttachEngine3D
  Height = 1.5
  Radius = 0.9
FEATURE [Part::Cut] Cut157
  Base = -> Cylinder278
  Placement = pos=(12.7,0,0) rot=(0,0,1;0rad)
  Tool = -> Cylinder263
FEATURE [Part::Cylinder] Cylinder279
  Angle = 360
  AttacherType = Attacher::AttachEngine3D
  Height = 1.5
  Radius = 0.9
FEATURE [Part::Cylinder] Cylinder280
  Angle = 360
  AttacherType = Attacher::AttachEngine3D
  Height = 1.5
  Radius = 0.4
FEATURE [Part::Cylinder] Cylinder281
  Angle = 360
  AttacherType = Attacher::AttachEngine3D
  Height = 1.5
  Radius = 0.4
FEATURE [Part::Cylinder] Cylinder282
  Angle = 360
  AttacherType = Attacher::AttachEngine3D
  Height = 1.5
  Radius = 0.9
FEATURE [Part::Cylinder] Cylinder283 .. Cylinder288  x6 (patterned run collapsed; names and placements below)
  Angle = 360
  AttacherType = Attacher::AttachEngine3D
  Height = 1.5
  Radius = 0.4
FEATURE [Part::Cylinder] Cylinder289
  Angle = 360
  AttacherType = Attacher::AttachEngine3D
  Height = 1.5
  Radius = 0.9
FEATURE [Part::Cylinder] Cylinder290
  Angle = 360
  AttacherType = Attacher::AttachEngine3D
  Height = 1.5
  Radius = 0.9
FEATURE [Part::Cut] Cut154
  Base = -> Cylinder290
  Placement = pos=(17.78,0,0) rot=(0,0,1;0rad)
  Tool = -> Cylinder264
FEATURE [Part::Cylinder] Cylinder291
  Angle = 360
  AttacherType = Attacher::AttachEngine3D
  Height = 1.5
  Radius = 0.4
FEATURE [Part::Cylinder] Cylinder292
  Angle = 360
  AttacherType = Attacher::AttachEngine3D
  Height = 1.5
  Radius = 0.9
FEATURE [Part::Cylinder] Cylinder293
  Angle = 360
  AttacherType = Attacher::AttachEngine3D
  Height = 1.5
  Radius = 0.4
FEATURE [Part::Cylinder] Cylinder294
  Angle = 360
  AttacherType = Attacher::AttachEngine3D
  Height = 1.5
  Radius = 0.9
FEATURE [Part::Cut] Cut152
  Base = -> Cylinder294
  Placement = pos=(7.62,0,0) rot=(0,0,1;0rad)
  Tool = -> Cylinder280
FEATURE [Part::Cylinder] Cylinder295
  Angle = 360
  AttacherType = Attacher::AttachEngine3D
  Height = 1.5
  Radius = 0.4
FEATURE [Part::Cylinder] Cylinder296
  Angle = 360
  AttacherType = Attacher::AttachEngine3D
  Height = 1.5
  Radius = 0.4
FEATURE [Part::Cut] Cut151
  Base = -> Cylinder260
  Placement = pos=(15.24,0,0) rot=(0,0,1;0rad)
  Tool = -> Cylinder296
FEATURE [Part::Box] Box233  label="Cube211"
  AttacherType = Attacher::AttachEngine3D
  Height = 1.5
  Length = 1.8
  Placement = pos=(-0.9,-0.9,0) rot=(0,0,1;0rad)
  Width = 1.8
FEATURE [Part::Cylinder] Cylinder297
  Angle = 360
  AttacherType = Attacher::AttachEngine3D
  Height = 1.5
  Radius = 0.4
FEATURE [Part::Cylinder] Cylinder298
  Angle = 360
  AttacherType = Attacher::AttachEngine3D
  Height = 1.5
  Radius = 0.9
FEATURE [Part::Cut] Cut153
  Base = -> Cylinder298
  Placement = pos=(5.08,0,0) rot=(0,0,1;0rad)
  Tool = -> Cylinder288
FEATURE [Part::Cylinder] Cylinder299
  Angle = 360
  AttacherType = Attacher::AttachEngine3D
  Height = 1.5
  Radius = 0.4
FEATURE [Part::Cylinder] Cylinder300
  Angle = 360
  AttacherType = Attacher::AttachEngine3D
  Height = 1.5
  Radius = 0.9
FEATURE [Part::Cylinder] Cylinder301
  Angle = 360
  AttacherType = Attacher::AttachEngine3D
  Height = 1.5
  Radius = 0.4
FEATURE [Part::Cylinder] Cylinder302
  Angle = 360
  AttacherType = Attacher::AttachEngine3D
  Height = 1.5
  Radius = 0.9
FEATURE [Part::Cylinder] Cylinder303
  Angle = 360
  AttacherType = Attacher::AttachEngine3D
  Height = 1.5
  Radius = 0.9
FEATURE [Mesh::Feature] __54_pin_header011  label="2.54_pin_header011"
  Placement = pos=(21.2,27.2,-0.8) rot=(0,0,1;0rad)
FEATURE [Part::Cut] Cut163
  Base = -> Cylinder282
  Placement = pos=(17.78,0,0) rot=(0,0,1;0rad)
  Tool = -> Cylinder287
FEATURE [Part::Cut] Cut167
  Base = -> Cylinder302
  Placement = pos=(7.62,0,0) rot=(0,0,1;0rad)
  Tool = -> Cylinder299
FEATURE [Part::Cut] Cut169
  Base = -> Cylinder289
  Placement = pos=(10.16,0,0) rot=(0,0,1;0rad)
  Tool = -> Cylinder291
FEATURE [Part::Cut] Cut170
  Base = -> Cylinder254
  Placement = pos=(22.86,0,0) rot=(0,0,1;0rad)
  Tool = -> Cylinder259
FEATURE [Part::Cut] Cut171
  Base = -> Cylinder279
  Placement = pos=(12.7,0,0) rot=(0,0,1;0rad)
  Tool = -> Cylinder284
FEATURE [Part::Cut] Cut172
  Base = -> Cylinder303
  Placement = pos=(2.54,0,0) rot=(0,0,1;0rad)
  Tool = -> Cylinder295
FEATURE [Part::Cut] Cut175
  Base = -> Cylinder292
  Placement = pos=(5.08,0,0) rot=(0,0,1;0rad)
  Tool = -> Cylinder301
FEATURE [Part::Cut] Cut176
  Base = -> Cylinder300
  Placement = pos=(20.32,0,0) rot=(0,0,1;0rad)
  Tool = -> Cylinder293
FEATURE [Part::Compound] Compound132  label="contact row 008"
  Links = -> [Cut170,Cut158,Cut154,Cut151,Cut152,Cut153,Cut172,Cut169,Cut176,Cut171]
  Placement = pos=(8.5,1.73,0) rot=(0,0,1;0rad)
FEATURE [Part::Cut] Cut182
  Base = -> Box233
  Tool = -> Cylinder273
FEATURE [Part::Compound] Compound126  label="contact row 005"
  Links = -> [Cut182,Cut159,Cut155,Cut149,Cut148,Cut156,Cut150,Cut161,Cut157,Cut162]
  Placement = pos=(8.5,4.27,0) rot=(0,0,1;0rad)
FEATURE [Part::Cylinder] Cylinder304
  Angle = 360
  AttacherType = Attacher::AttachEngine3D
  Height = 1.5
  Radius = 0.4
FEATURE [Part::Cylinder] Cylinder305
  Angle = 360
  AttacherType = Attacher::AttachEngine3D
  Height = 1.5
  Radius = 0.4
FEATURE [Part::Cylinder] Cylinder306
  Angle = 360
  AttacherType = Attacher::AttachEngine3D
  Height = 1.5
  Radius = 0.9
FEATURE [Part::Cut] Cut179
  Base = -> Cylinder306
  Placement = pos=(12.7,0,0) rot=(0,0,1;0rad)
  Tool = -> Cylinder283
FEATURE [Part::Cylinder] Cylinder307
  Angle = 360
  AttacherType = Attacher::AttachEngine3D
  Height = 1.5
  Radius = 0.4
FEATURE [Part::Cylinder] Cylinder308
  Angle = 360
  AttacherType = Attacher::AttachEngine3D
  Height = 1.5
  Radius = 0.9
FEATURE [Part::Cut] Cut180
  Base = -> Cylinder308
  Placement = pos=(10.16,0,0) rot=(0,0,1;0rad)
  Tool = -> Cylinder285
FEATURE [Part::Cylinder] Cylinder309
  Angle = 360
  AttacherType = Attacher::AttachEngine3D
  Height = 1.5
  Radius = 0.9
FEATURE [Part::Cylinder] Cylinder310
  Angle = 360
  AttacherType = Attacher::AttachEngine3D
  Height = 1.5
  Placement = pos=(12.7,0,0) rot=(0,0,1;0rad)
  Radius = 0.9
FEATURE [Part::Cylinder] Cylinder311
  Angle = 360
  AttacherType = Attacher::AttachEngine3D
  Height = 1.5
  Placement = pos=(2.54,0,0) rot=(0,0,1;0rad)
  Radius = 0.9
FEATURE [Part::Cylinder] Cylinder312
  Angle = 360
  AttacherType = Attacher::AttachEngine3D
  Height = 1.5
  Radius = 0.9
FEATURE [Part::Cut] Cut174
  Base = -> Cylinder312
  Placement = pos=(2.54,0,0) rot=(0,0,1;0rad)
  Tool = -> Cylinder297
FEATURE [Part::Cylinder] Cylinder313
  Angle = 360
  AttacherType = Attacher::AttachEngine3D
  Height = 1.5
  Radius = 0.9
FEATURE [Part::Cut] Cut181
  Base = -> Cylinder313
  Placement = pos=(15.24,0,0) rot=(0,0,1;0rad)
  Tool = -> Cylinder281
FEATURE [Part::Cylinder] Cylinder314
  Angle = 360
  AttacherType = Attacher::AttachEngine3D
  Height = 1.5
  Radius = 0.9
FEATURE [Part::Cut] Cut173
  Base = -> Cylinder314
  Placement = pos=(20.32,0,0) rot=(0,0,1;0rad)
  Tool = -> Cylinder286
FEATURE [Part::Cylinder] Cylinder315
  Angle = 360
  AttacherType = Attacher::AttachEngine3D
  Height = 1.5
  Radius = 0.9
FEATURE [Part::Cylinder] Cylinder316
  Angle = 360
  AttacherType = Attacher::AttachEngine3D
  Height = 1.5
  Radius = 0.4
FEATURE [Part::Cylinder] Cylinder317
  Angle = 360
  AttacherType = Attacher::AttachEngine3D
  Height = 1.5
  Radius = 0.9
FEATURE [Part::Cylinder] Cylinder318
  Angle = 360
  AttacherType = Attacher::AttachEngine3D
  Height = 1.5
  Radius = 0.9
FEATURE [Part::Cylinder] Cylinder319
  Angle = 360
  AttacherType = Attacher::AttachEngine3D
  Height = 1.5
  Radius = 0.9
FEATURE [Part::Cylinder] Cylinder320
  Angle = 360
  AttacherType = Attacher::AttachEngine3D
  Height = 1.5
  Radius = 0.4
FEATURE [Part::Cut] Cut164
  Base = -> Cylinder318
  Tool = -> Cylinder320
FEATURE [Part::Box] Box234  label="Cube212"
  AttacherType = Attacher::AttachEngine3D
  Height = 1.5
  Length = 1.8
  Placement = pos=(-0.9,-0.9,0) rot=(0,0,1;0rad)
  Width = 1.8
FEATURE [Part::Cylinder] Cylinder321
  Angle = 360
  AttacherType = Attacher::AttachEngine3D
  Height = 1.5
  Radius = 0.9
FEATURE [Part::Cylinder] Cylinder322
  Angle = 360
  AttacherType = Attacher::AttachEngine3D
  Height = 1.5
  Radius = 0.4
FEATURE [Part::Cut] Cut165
  Base = -> Cylinder309
  Placement = pos=(20.32,0,0) rot=(0,0,1;0rad)
  Tool = -> Cylinder322
FEATURE [Part::Cylinder] Cylinder323
  Angle = 360
  AttacherType = Attacher::AttachEngine3D
  Height = 1.5
  Radius = 0.9
FEATURE [Part::Cut] Cut177
  Base = -> Cylinder323
  Placement = pos=(15.24,0,0) rot=(0,0,1;0rad)
  Tool = -> Cylinder305
FEATURE [Part::Cylinder] Cylinder324
  Angle = 360
  AttacherType = Attacher::AttachEngine3D
  Height = 1.5
  Radius = 0.4
FEATURE [Part::Cut] Cut178
  Base = -> Cylinder319
  Placement = pos=(7.62,0,0) rot=(0,0,1;0rad)
  Tool = -> Cylinder324
FEATURE [Part::Cylinder] Cylinder325
  Angle = 360
  AttacherType = Attacher::AttachEngine3D
  Height = 1.5
  Radius = 0.4
FEATURE [Part::Cylinder] Cylinder326
  Angle = 360
  AttacherType = Attacher::AttachEngine3D
  Height = 1.5
  Radius = 0.4
FEATURE [Part::Cut] Cut166
  Base = -> Cylinder315
  Placement = pos=(22.86,0,0) rot=(0,0,1;0rad)
  Tool = -> Cylinder326
FEATURE [Part::Compound] Compound127  label="contact row 006"
  Links = -> [Cut166,Cut164,Cut163,Cut181,Cut167,Cut175,Cut174,Cut180,Cut173,Cut179]
  Placement = pos=(8.5,27.13,0) rot=(0,0,1;0rad)
FEATURE [Part::Cylinder] Cylinder327
  Angle = 360
  AttacherType = Attacher::AttachEngine3D
  Height = 1.5
  Radius = 0.4
FEATURE [Part::Cylinder] Cylinder328
  Angle = 360
  AttacherType = Attacher::AttachEngine3D
  Height = 1.5
  Radius = 0.9
FEATURE [Part::Cylinder] Cylinder329
  Angle = 360
  AttacherType = Attacher::AttachEngine3D
  Height = 1.5
  Radius = 0.9
FEATURE [Part::Cylinder] Cylinder330
  Angle = 360
  AttacherType = Attacher::AttachEngine3D
  Height = 1.5
  Radius = 0.4
FEATURE [Part::Cylinder] Cylinder331
  Angle = 360
  AttacherType = Attacher::AttachEngine3D
  Height = 1.5
  Radius = 0.9
FEATURE [Part::Cut] Cut168
  Base = -> Cylinder331
  Placement = pos=(17.78,0,0) rot=(0,0,1;0rad)
  Tool = -> Cylinder325
FEATURE [Part::Cylinder] Cylinder332
  Angle = 360
  AttacherType = Attacher::AttachEngine3D
  Height = 1.5
  Radius = 0.4
FEATURE [Part::Cylinder] Cylinder333
  Angle = 360
  AttacherType = Attacher::AttachEngine3D
  Height = 1.5
  Radius = 0.9
FEATURE [Part::Cylinder] Cylinder334
  Angle = 360
  AttacherType = Attacher::AttachEngine3D
  Height = 1.5
  Placement = pos=(5.08,0,0) rot=(0,0,1;0rad)
  Radius = 0.9
FEATURE [Part::Cylinder] Cylinder335
  Angle = 360
  AttacherType = Attacher::AttachEngine3D
  Height = 1.5
  Placement = pos=(10.16,0,0) rot=(0,0,1;0rad)
  Radius = 0.9
FEATURE [Part::Cylinder] Cylinder336
  Angle = 360
  AttacherType = Attacher::AttachEngine3D
  Height = 1.5
  Placement = pos=(5.08,0,0) rot=(0,0,1;0rad)
  Radius = 0.9
FEATURE [Part::Cylinder] Cylinder337
  Angle = 360
  AttacherType = Attacher::AttachEngine3D
  Height = 1.5
  Placement = pos=(12.7,0,0) rot=(0,0,1;0rad)
  Radius = 0.9
FEATURE [Part::Cylinder] Cylinder338
  Angle = 360
  AttacherType = Attacher::AttachEngine3D
  Height = 1.5
  Placement = pos=(2.54,0,0) rot=(0,0,1;0rad)
  Radius = 0.9
FEATURE [Part::Cylinder] Cylinder339
  Angle = 360
  AttacherType = Attacher::AttachEngine3D
  Height = 1.5
  Placement = pos=(15.24,0,0) rot=(0,0,1;0rad)
  Radius = 0.9
FEATURE [Part::Cylinder] Cylinder340
  Angle = 360
  AttacherType = Attacher::AttachEngine3D
  Height = 1.5
  Placement = pos=(22.86,0,0) rot=(0,0,1;0rad)
  Radius = 0.9
FEATURE [Part::Cylinder] Cylinder341
  Angle = 360
  AttacherType = Attacher::AttachEngine3D
  Height = 1.5
  Placement = pos=(7.62,0,0) rot=(0,0,1;0rad)
  Radius = 0.9
FEATURE [Part::Cylinder] Cylinder342
  Angle = 360
  AttacherType = Attacher::AttachEngine3D
  Height = 1.5
  Radius = 0.9
FEATURE [Part::Cylinder] Cylinder343
  Angle = 360
  AttacherType = Attacher::AttachEngine3D
  Height = 1.5
  Placement = pos=(22.86,0,0) rot=(0,0,1;0rad)
  Radius = 0.9
FEATURE [Part::Cylinder] Cylinder344
  Angle = 360
  AttacherType = Attacher::AttachEngine3D
  Height = 1.5
  Placement = pos=(15.24,0,0) rot=(0,0,1;0rad)
  Radius = 0.9
FEATURE [Part::Cylinder] Cylinder345
  Angle = 360
  AttacherType = Attacher::AttachEngine3D
  Height = 1.5
  Placement = pos=(7.62,0,0) rot=(0,0,1;0rad)
  Radius = 0.9
FEATURE [Part::Cylinder] Cylinder346
  Angle = 360
  AttacherType = Attacher::AttachEngine3D
  Height = 1.5
  Placement = pos=(10.16,0,0) rot=(0,0,1;0rad)
  Radius = 0.9
FEATURE [Part::Box] Box235  label="Cube213"
  AttacherType = Attacher::AttachEngine3D
  Height = 1.5
  Length = 1.8
  Placement = pos=(-0.9,-0.9,0) rot=(0,0,1;0rad)
  Width = 1.8
FEATURE [Part::Cylinder] Cylinder347
  Angle = 360
  AttacherType = Attacher::AttachEngine3D
  Height = 1.5
  Placement = pos=(20.32,0,0) rot=(0,0,1;0rad)
  Radius = 0.9
FEATURE [Part::Cylinder] Cylinder348
  Angle = 360
  AttacherType = Attacher::AttachEngine3D
  Height = 1.5
  Placement = pos=(5.08,0,0) rot=(0,0,1;0rad)
  Radius = 0.9
FEATURE [Part::Cylinder] Cylinder349
  Angle = 360
  AttacherType = Attacher::AttachEngine3D
  Height = 1.5
  Placement = pos=(12.7,0,0) rot=(0,0,1;0rad)
  Radius = 0.9
FEATURE [Part::Cylinder] Cylinder350
  Angle = 360
  AttacherType = Attacher::AttachEngine3D
  Height = 1.5
  Placement = pos=(10.16,0,0) rot=(0,0,1;0rad)
  Radius = 0.9
FEATURE [Part::Cylinder] Cylinder351
  Angle = 360
  AttacherType = Attacher::AttachEngine3D
  Height = 1.5
  Placement = pos=(2.54,0,0) rot=(0,0,1;0rad)
  Radius = 0.9
FEATURE [Part::Cylinder] Cylinder352
  Angle = 360
  AttacherType = Attacher::AttachEngine3D
  Height = 1.5
  Placement = pos=(17.78,0,0) rot=(0,0,1;0rad)
  Radius = 0.9
FEATURE [Part::Compound] Compound130  label="Compound157"
  Links = -> [Cylinder342,Cylinder336,Cylinder337,Cylinder346,Cylinder338,Cylinder341,Cylinder343,Cylinder344,Cylinder352,Cylinder347]
  Placement = pos=(8.5,1.73,0) rot=(0,0,1;0rad)
FEATURE [Part::Cylinder] Cylinder353
  Angle = 360
  AttacherType = Attacher::AttachEngine3D
  Height = 1.5
  Placement = pos=(17.78,0,0) rot=(0,0,1;0rad)
  Radius = 0.9
FEATURE [Part::Cylinder] Cylinder354
  Angle = 360
  AttacherType = Attacher::AttachEngine3D
  Height = 1.5
  Placement = pos=(20.32,0,0) rot=(0,0,1;0rad)
  Radius = 0.9
FEATURE [Part::Compound] Compound129
  Links = -> [Cylinder340,Cylinder334,Cylinder310,Cylinder335,Cylinder311,Cylinder345,Cylinder339,Cylinder353,Cylinder354,Box235]
  Placement = pos=(8.5,4.27,0) rot=(0,0,1;0rad)
FEATURE [Part::Cut] Cut187
  Base = -> Cylinder317
  Placement = pos=(5.08,0,0) rot=(0,0,1;0rad)
  Tool = -> Cylinder327
FEATURE [Part::Cut] Cut189
  Base = -> Box234
  Tool = -> Cylinder307
FEATURE [Part::Cut] Cut190
  Base = -> Cylinder321
  Placement = pos=(22.86,0,0) rot=(0,0,1;0rad)
  Tool = -> Cylinder304
FEATURE [Part::Cut] Cut192
  Base = -> Cylinder328
  Placement = pos=(2.54,0,0) rot=(0,0,1;0rad)
  Tool = -> Cylinder316
FEATURE [Part::Cut] Cut195
  Base = -> Cylinder329
  Placement = pos=(10.16,0,0) rot=(0,0,1;0rad)
  Tool = -> Cylinder332
FEATURE [Part::Cut] Cut196
  Base = -> Cylinder333
  Placement = pos=(12.7,0,0) rot=(0,0,1;0rad)
  Tool = -> Cylinder330
FEATURE [Part::Compound] Compound128  label="contact row 007"
  Links = -> [Cut189,Cut165,Cut168,Cut177,Cut178,Cut187,Cut192,Cut195,Cut196,Cut190]
  Placement = pos=(8.5,29.67,0) rot=(0,0,1;0rad)
FEATURE [Part::Cylinder] Cylinder355
  Angle = 360
  AttacherType = Attacher::AttachEngine3D
  Height = 1.5
  Placement = pos=(20.32,0,0) rot=(0,0,1;0rad)
  Radius = 0.9
FEATURE [Part::Cylinder] Cylinder356
  Angle = 360
  AttacherType = Attacher::AttachEngine3D
  Height = 1.5
  Placement = pos=(10.16,0,0) rot=(0,0,1;0rad)
  Radius = 0.9
FEATURE [Part::Cylinder] Cylinder357
  Angle = 360
  AttacherType = Attacher::AttachEngine3D
  Height = 1.3
  Placement = pos=(-7,1.3,-17) rot=(1,0,0;1.5708rad)
  Radius = 0.9
FEATURE [Part::Box] Box236  label="Cube214"
  AttacherType = Attacher::AttachEngine3D
  Height = 36.5
  Length = 24.5
  Placement = pos=(-24.5,0,-19.5) rot=(0,0,1;0rad)
  Width = 1.3
FEATURE [Part::Cylinder] Cylinder358
  Angle = 360
  AttacherType = Attacher::AttachEngine3D
  Height = 10
  Placement = pos=(-14.5,2,14) rot=(1,0,0;1.5708rad)
  Radius = 2
FEATURE [Part::Cylinder] Cylinder359
  Angle = 360
  AttacherType = Attacher::AttachEngine3D
  Height = 1.3
  Placement = pos=(-9.54,1.3,-17) rot=(1,0,0;1.5708rad)
  Radius = 0.9
FEATURE [Part::Cylinder] Cylinder360
  Angle = 360
  AttacherType = Attacher::AttachEngine3D
  Height = 10
  Placement = pos=(-21.5,2,-16.5) rot=(1,0,0;1.5708rad)
  Radius = 2
FEATURE [Part::Cylinder] Cylinder361
  Angle = 360
  AttacherType = Attacher::AttachEngine3D
  Height = 1.5
  Radius = 0.9
FEATURE [Part::Cylinder] Cylinder362
  Angle = 360
  AttacherType = Attacher::AttachEngine3D
  Height = 1.5
  Placement = pos=(17.78,0,0) rot=(0,0,1;0rad)
  Radius = 0.9
FEATURE [Part::Cylinder] Cylinder363
  Angle = 360
  AttacherType = Attacher::AttachEngine3D
  Height = 1.3
  Radius = 0.9
FEATURE [Part::Cylinder] Cylinder364
  Angle = 360
  AttacherType = Attacher::AttachEngine3D
  Height = 1.3
  Placement = pos=(-12.08,1.3,-17) rot=(1,0,0;1.5708rad)
  Radius = 0.9
FEATURE [Part::Cylinder] Cylinder365
  Angle = 360
  AttacherType = Attacher::AttachEngine3D
  Height = 1.3
  Radius = 0.4
FEATURE [Part::Cylinder] Cylinder366
  Angle = 360
  AttacherType = Attacher::AttachEngine3D
  Height = 1.5
  Placement = pos=(5.08,0,0) rot=(0,0,1;0rad)
  Radius = 0.9
FEATURE [Part::Box] Box237  label="Cube215"
  AttacherType = Attacher::AttachEngine3D
  Height = 1.5
  Length = 1.8
  Placement = pos=(-0.9,-0.9,0) rot=(0,0,1;0rad)
  Width = 1.8
FEATURE [Part::Cylinder] Cylinder367
  Angle = 360
  AttacherType = Attacher::AttachEngine3D
  Height = 1.3
  Radius = 0.4
FEATURE [Part::Cylinder] Cylinder368
  Angle = 360
  AttacherType = Attacher::AttachEngine3D
  Height = 1.3
  Placement = pos=(-14.62,1.3,-17) rot=(1,0,0;1.5708rad)
  Radius = 0.9
FEATURE [Part::Cylinder] Cylinder369
  Angle = 360
  AttacherType = Attacher::AttachEngine3D
  Height = 1.3
  Radius = 0.9
FEATURE [Part::Cylinder] Cylinder370
  Angle = 360
  AttacherType = Attacher::AttachEngine3D
  Height = 1.5
  Placement = pos=(7.62,0,0) rot=(0,0,1;0rad)
  Radius = 0.9
FEATURE [Part::Cylinder] Cylinder371
  Angle = 360
  AttacherType = Attacher::AttachEngine3D
  Height = 1.5
  Placement = pos=(15.24,0,0) rot=(0,0,1;0rad)
  Radius = 0.9
FEATURE [Part::Cylinder] Cylinder372
  Angle = 360
  AttacherType = Attacher::AttachEngine3D
  Height = 1.5
  Placement = pos=(22.86,0,0) rot=(0,0,1;0rad)
  Radius = 0.9
FEATURE [Part::Cylinder] Cylinder373
  Angle = 360
  AttacherType = Attacher::AttachEngine3D
  Height = 1.5
  Placement = pos=(12.7,0,0) rot=(0,0,1;0rad)
  Radius = 0.9
FEATURE [Part::Cylinder] Cylinder374
  Angle = 360
  AttacherType = Attacher::AttachEngine3D
  Height = 1.5
  Placement = pos=(15.24,0,0) rot=(0,0,1;0rad)
  Radius = 0.9
FEATURE [Part::Cylinder] Cylinder375
  Angle = 360
  AttacherType = Attacher::AttachEngine3D
  Height = 1.5
  Placement = pos=(17.78,0,0) rot=(0,0,1;0rad)
  Radius = 0.9
FEATURE [Part::Cylinder] Cylinder376
  Angle = 360
  AttacherType = Attacher::AttachEngine3D
  Height = 1.5
  Placement = pos=(20.32,0,0) rot=(0,0,1;0rad)
  Radius = 0.9
FEATURE [Part::Cylinder] Cylinder377
  Angle = 360
  AttacherType = Attacher::AttachEngine3D
  Height = 1.3
  Radius = 0.9
FEATURE [Part::Cut] Cut193  label="contact011"
  Base = -> Cylinder377
  Placement = pos=(-7,1.3,-17) rot=(1,0,0;1.5708rad)
  Tool = -> Cylinder367
FEATURE [Part::Cylinder] Cylinder378
  Angle = 360
  AttacherType = Attacher::AttachEngine3D
  Height = 1.5
  Placement = pos=(22.86,0,0) rot=(0,0,1;0rad)
  Radius = 0.9
FEATURE [Part::Compound] Compound151  label="Compound156"
  Links = -> [Cylinder361,Cylinder348,Cylinder349,Cylinder350,Cylinder351,Cylinder370,Cylinder378,Cylinder371,Cylinder362,Cylinder355]
  Placement = pos=(8.5,27.13,0) rot=(0,0,1;0rad)
FEATURE [Part::Cylinder] Cylinder379
  Angle = 360
  AttacherType = Attacher::AttachEngine3D
  Height = 1.5
  Placement = pos=(2.54,0,0) rot=(0,0,1;0rad)
  Radius = 0.9
FEATURE [Part::Cylinder] Cylinder380
  Angle = 360
  AttacherType = Attacher::AttachEngine3D
  Height = 1.5
  Placement = pos=(7.62,0,0) rot=(0,0,1;0rad)
  Radius = 0.9
FEATURE [Part::Compound] Compound141  label="Compound174"
  Links = -> [Cylinder372,Cylinder366,Cylinder373,Cylinder356,Cylinder379,Cylinder380,Cylinder374,Cylinder375,Cylinder376,Box237]
  Placement = pos=(8.5,29.67,0) rot=(0,0,1;0rad)
FEATURE [Part::MultiFuse] Fusion062
  Shapes = -> [Compound129,Compound141,Compound130,Compound151]
FEATURE [Part::Cut] Cut183  label="PCB with holes001"
  Base = -> Cut160
  Tool = -> Fusion062
FEATURE [Part::Compound] Compound149  label="Compound173"
  Links = -> [Box229,Box230,Box231,__54_pin_header009,_73460003,Box232,Cut183,Compound132,Compound126,__54_pin_header010,Compound127,__54_pin_header008,__54_pin_header011,Compound128]
  Placement = pos=(0,0,0) rot=(0,1,0;1.5708rad)
FEATURE [Part::MultiFuse] Fusion063  label="ESP32 mini kit001"
  Placement = pos=(17,2,75) rot=(0,0,1;1.5708rad)
  Shapes = -> [Compound149]
FEATURE [Part::Cylinder] Cylinder381
  Angle = 360
  AttacherType = Attacher::AttachEngine3D
  Height = 1.3
  Placement = pos=(-17.16,1.3,-17) rot=(1,0,0;1.5708rad)
  Radius = 0.9
FEATURE [Part::MultiFuse] Fusion064
  Shapes = -> [Cylinder357,Cylinder368,Cylinder364,Cylinder381,Cylinder359]
FEATURE [Part::Cylinder] Cylinder382
  Angle = 360
  AttacherType = Attacher::AttachEngine3D
  Height = 10
  Placement = pos=(-3,2,14) rot=(1,0,0;1.5708rad)
  Radius = 2
FEATURE [Part::Cylinder] Cylinder383
  Angle = 360
  AttacherType = Attacher::AttachEngine3D
  Height = 10
  Placement = pos=(-21.5,2,14) rot=(1,0,0;1.5708rad)
  Radius = 2
FEATURE [Part::Cylinder] Cylinder384
  Angle = 360
  AttacherType = Attacher::AttachEngine3D
  Height = 10
  Placement = pos=(-3,2,-16.5) rot=(1,0,0;1.5708rad)
  Radius = 2
FEATURE [Part::Box] Box238  label="Cube216"
  AttacherType = Attacher::AttachEngine3D
  Height = 12
  Length = 16
  Placement = pos=(-18,1.3,-6) rot=(0,0,1;0rad)
  Width = 3
FEATURE [Part::Fillet] Fillet030  label="neo6m chip001"
  Base = -> Box238
  Edges = 4 edges r=0.5: [Edge3,Edge7,Edge11,Edge12]
FEATURE [Part::Cylinder] Cylinder385
  Angle = 360
  AttacherType = Attacher::AttachEngine3D
  Height = 1.3
  Radius = 0.4
FEATURE [Part::Cut] Cut184  label="contact006"
  Base = -> Cylinder369
  Placement = pos=(-9.54,1.3,-17) rot=(1,0,0;1.5708rad)
  Tool = -> Cylinder385
FEATURE [Part::Cylinder] Cylinder386
  Angle = 360
  AttacherType = Attacher::AttachEngine3D
  Height = 1.3
  Radius = 0.4
FEATURE [Part::Cut] Cut186  label="contact008"
  Base = -> Cylinder363
  Placement = pos=(-12.08,1.3,-17) rot=(1,0,0;1.5708rad)
  Tool = -> Cylinder386
FEATURE [Part::Cylinder] Cylinder387
  Angle = 360
  AttacherType = Attacher::AttachEngine3D
  Height = 1.3
  Radius = 0.4
FEATURE [Part::Cylinder] Cylinder388
  Angle = 360
  AttacherType = Attacher::AttachEngine3D
  Height = 1.3
  Radius = 0.9
FEATURE [Part::Cut] Cut185  label="contact007"
  Base = -> Cylinder388
  Placement = pos=(-14.62,1.3,-17) rot=(1,0,0;1.5708rad)
  Tool = -> Cylinder387
FEATURE [Part::Box] Box239  label="Cube217"
  AttacherType = Attacher::AttachEngine3D
  Height = 2.54
  Length = 2.54
  Width = 2.54
FEATURE [Part::Chamfer] Chamfer041  label="Chamfer061"
  Base = -> Box239
  Edges = 4 edges r=0.5: [Edge2,Edge4,Edge6,Edge8]
FEATURE [Part::Box] Box240  label="Cube218"
  AttacherType = Attacher::AttachEngine3D
  Height = 2.54
  Length = 2.54
  Width = 2.54
FEATURE [Part::Chamfer] Chamfer045  label="Chamfer064"
  Base = -> Box240
  Edges = 4 edges r=0.5: [Edge2,Edge4,Edge6,Edge8]
FEATURE [Part::Cylinder] Cylinder389
  Angle = 360
  AttacherType = Attacher::AttachEngine3D
  Height = 1.3
  Radius = 0.4
FEATURE [Part::Box] Box241  label="Cube219"
  AttacherType = Attacher::AttachEngine3D
  Height = 1
  Length = 1
  Placement = pos=(0.77,-5,0.77) rot=(0,0,1;0rad)
  Width = 10
FEATURE [Part::Box] Box242  label="Cube220"
  AttacherType = Attacher::AttachEngine3D
  Height = 1
  Length = 1
  Placement = pos=(0.77,-5,0.77) rot=(0,0,1;0rad)
  Width = 10
FEATURE [Part::Box] Box243  label="Cube221"
  AttacherType = Attacher::AttachEngine3D
  Height = 1
  Length = 1
  Placement = pos=(0.77,-5,0.77) rot=(0,0,1;0rad)
  Width = 10
FEATURE [Part::Box] Box244  label="Cube222"
  AttacherType = Attacher::AttachEngine3D
  Height = 1
  Length = 1
  Placement = pos=(0.77,-5,0.77) rot=(0,0,1;0rad)
  Width = 10
FEATURE [Part::Box] Box245  label="Cube223"
  AttacherType = Attacher::AttachEngine3D
  Height = 11
  Length = 2.54
  Placement = pos=(-1.27,-8.3,2) rot=(0,0,1;0rad)
  Width = 2.54
FEATURE [Part::Box] Box246  label="Cube224"
  AttacherType = Attacher::AttachEngine3D
  Height = 2.54
  Length = 2.54
  Width = 2.54
FEATURE [Part::Chamfer] Chamfer043  label="Chamfer062"
  Base = -> Box246
  Edges = 4 edges r=0.5: [Edge2,Edge4,Edge6,Edge8]
FEATURE [Part::Box] Box247  label="Cube225"
  AttacherType = Attacher::AttachEngine3D
  Height = 2.54
  Length = 2.54
  Width = 2.54
FEATURE [Part::Chamfer] Chamfer049
  Base = -> Box247
  Edges = 4 edges r=0.5: [Edge2,Edge4,Edge6,Edge8]
FEATURE [Part::Box] Box248  label="Cube226"
  AttacherType = Attacher::AttachEngine3D
  Height = 2.54
  Length = 2.54
  Width = 2.54
FEATURE [Part::Chamfer] Chamfer044  label="Chamfer063"
  Base = -> Box248
  Edges = 4 edges r=0.5: [Edge2,Edge4,Edge6,Edge8]
FEATURE [Part::Box] Box249  label="Cube227"
  AttacherType = Attacher::AttachEngine3D
  Height = 11
  Length = 2.54
  Placement = pos=(-1.27,-8.3,2) rot=(0,0,1;0rad)
  Width = 2.54
FEATURE [Part::Box] Box250  label="Cube228"
  AttacherType = Attacher::AttachEngine3D
  Height = 1
  Length = 1
  Placement = pos=(0.77,-5,0.77) rot=(0,0,1;0rad)
  Width = 10
FEATURE [Part::Compound] Compound153  label="straight pin + connector022"
  Links = -> [Box250,Chamfer045]
  Placement = pos=(0,0,2.54) rot=(0,0,1;0rad)
FEATURE [Part::Cylinder] Cylinder390
  Angle = 360
  AttacherType = Attacher::AttachEngine3D
  Height = 1.3
  Radius = 0.9
FEATURE [Part::Cut] Cut191  label="contact010"
  Base = -> Cylinder390
  Placement = pos=(-7,1.3,-17) rot=(1,0,0;1.5708rad)
  Tool = -> Cylinder389
FEATURE [Part::Cylinder] Cylinder391
  Angle = 360
  AttacherType = Attacher::AttachEngine3D
  Height = 1.3
  Radius = 0.9
FEATURE [Part::Cut] Cut188  label="contact009"
  Base = -> Cylinder391
  Placement = pos=(-17.16,1.3,-17) rot=(1,0,0;1.5708rad)
  Tool = -> Cylinder365
FEATURE [Part::Box] Box251  label="Cube229"
  AttacherType = Attacher::AttachEngine3D
  Height = 1
  Length = 1
  Placement = pos=(0.77,-5,0.77) rot=(0,0,1;0rad)
  Width = 10
FEATURE [Part::Compound] Compound145  label="straight pin007"
  Links = -> [Box251,Chamfer043]
  Placement = pos=(0,0,12.7) rot=(0,0,1;0rad)
FEATURE [Part::Box] Box252  label="Cube230"
  AttacherType = Attacher::AttachEngine3D
  Height = 2.54
  Length = 2.54
  Width = 2.54
FEATURE [Part::Chamfer] Chamfer038  label="Chamfer055"
  Base = -> Box252
  Edges = 4 edges r=0.5: [Edge2,Edge4,Edge6,Edge8]
FEATURE [Part::Box] Box253  label="Cube231"
  AttacherType = Attacher::AttachEngine3D
  Height = 1
  Length = 1
  Placement = pos=(0.77,-5,0.77) rot=(0,0,1;0rad)
  Width = 10
FEATURE [Part::Box] Box254  label="Cube232"
  AttacherType = Attacher::AttachEngine3D
  Height = 2.54
  Length = 2.54
  Width = 2.54
FEATURE [Part::Chamfer] Chamfer046  label="Chamfer065"
  Base = -> Box254
  Edges = 4 edges r=0.5: [Edge2,Edge4,Edge6,Edge8]
FEATURE [Part::Compound] Compound136  label="straight pin006"
  Links = -> [Box244,Chamfer046]
  Placement = pos=(0,0,15.24) rot=(0,0,1;0rad)
FEATURE [Part::Box] Box255  label="Cube233"
  AttacherType = Attacher::AttachEngine3D
  Height = 2.54
  Length = 2.54
  Placement = pos=(0,-11,0) rot=(0,0,1;0rad)
  Width = 11
FEATURE [Part::Compound] Compound144  label="straight pin + connector019"
  Links = -> [Box243,Chamfer038,Box255]
  Placement = pos=(0,0,7.62) rot=(0,0,1;0rad)
FEATURE [Part::Box] Box256  label="Cube234"
  AttacherType = Attacher::AttachEngine3D
  Height = 2.54
  Length = 2.54
  Width = 2.54
FEATURE [Part::Chamfer] Chamfer037  label="Chamfer054"
  Base = -> Box256
  Edges = 4 edges r=0.5: [Edge2,Edge4,Edge6,Edge8]
FEATURE [Part::Compound] Compound143  label="straight pin 003"
  Links = -> [Box241,Chamfer037]
  Placement = pos=(0,0,5.08) rot=(0,0,1;0rad)
FEATURE [Part::Box] Box257  label="Cube235"
  AttacherType = Attacher::AttachEngine3D
  Height = 2.54
  Length = 2.54
  Placement = pos=(0,-11,0) rot=(0,0,1;0rad)
  Width = 11
FEATURE [Part::Compound] Compound142  label="straight pin + connector018"
  Links = -> [Box253,Chamfer041,Box257]
  Placement = pos=(0,0,10.16) rot=(0,0,1;0rad)
FEATURE [Part::Box] Box258  label="Cube236"
  AttacherType = Attacher::AttachEngine3D
  Height = 2.54
  Length = 2.54
  Placement = pos=(0,-11,0) rot=(0,0,1;0rad)
  Width = 11
FEATURE [Part::Box] Box259  label="Cube237"
  AttacherType = Attacher::AttachEngine3D
  Height = 1
  Length = 1
  Placement = pos=(0.77,-5,0.77) rot=(0,0,1;0rad)
  Width = 10
FEATURE [Part::Compound] Compound152  label="straight pin + connector021"
  Links = -> [Box259,Chamfer044,Box258]
  Placement = pos=(0,0,17.78) rot=(0,0,1;0rad)
FEATURE [Part::Box] Box260  label="connectors ESP033"
  AttacherType = Attacher::AttachEngine3D
  Height = 20.32
  Length = 11
  Placement = pos=(-7,6.38,47.5) rot=(0,0,1;0rad)
  Width = 2.54
FEATURE [Part::Box] Box261  label="Cube238"
  AttacherType = Attacher::AttachEngine3D
  Height = 2.54
  Length = 2.54
  Placement = pos=(0,-11,0) rot=(0,0,1;0rad)
  Width = 11
FEATURE [Part::Compound] Compound150  label="straight pin + connector020"
  Links = -> [Box242,Chamfer049,Box261]
FEATURE [Part::Compound] Compound147  label="pins ESP033"
  Links = -> [Compound150,Compound152,Compound144,Compound145,Compound142,Compound153,Compound143,Compound136]
  Placement = pos=(12.75,-0.5,47.45) rot=(0,0,1;0rad)
FEATURE [Part::Box] Box262  label="Cube239"
  AttacherType = Attacher::AttachEngine3D
  Height = 11
  Length = 2.54
  Placement = pos=(-1.27,-8.3,2) rot=(0,0,1;0rad)
  Width = 2.54
FEATURE [Part::Box] Box263  label="Cube240"
  AttacherType = Attacher::AttachEngine3D
  Height = 1
  Length = 1
  Placement = pos=(0.77,-5,0.77) rot=(0,0,1;0rad)
  Width = 10
FEATURE [Part::Box] Box264  label="Cube241"
  AttacherType = Attacher::AttachEngine3D
  Height = 2.54
  Length = 2.54
  Width = 2.54
FEATURE [Part::Chamfer] Chamfer051  label="Chamfer068"
  Base = -> Box264
  Edges = 4 edges r=0.5: [Edge2,Edge4,Edge6,Edge8]
FEATURE [Part::Box] Box265  label="Cube242"
  AttacherType = Attacher::AttachEngine3D
  Height = 2.54
  Length = 2.54
  Width = 2.54
FEATURE [Part::Chamfer] Chamfer050  label="Chamfer067"
  Base = -> Box265
  Edges = 4 edges r=0.5: [Edge2,Edge4,Edge6,Edge8]
FEATURE [Part::Box] Box266  label="Cube243"
  AttacherType = Attacher::AttachEngine3D
  Height = 1
  Length = 1
  Placement = pos=(0.77,-5,0.77) rot=(0,0,1;0rad)
  Width = 10
FEATURE [Part::Box] Box267  label="Cube244"
  AttacherType = Attacher::AttachEngine3D
  Height = 2.54
  Length = 2.54
  Width = 2.54
FEATURE [Part::Chamfer] Chamfer053  label="Chamfer070"
  Base = -> Box267
  Edges = 4 edges r=0.5: [Edge2,Edge4,Edge6,Edge8]
FEATURE [Part::Box] Box268  label="Cube245"
  AttacherType = Attacher::AttachEngine3D
  Height = 2.54
  Length = 2.54
  Width = 2.54
FEATURE [Part::Chamfer] Chamfer039  label="Chamfer060"
  Base = -> Box268
  Edges = 4 edges r=0.5: [Edge2,Edge4,Edge6,Edge8]
FEATURE [Part::Box] Box269  label="Cube246"
  AttacherType = Attacher::AttachEngine3D
  Height = 2.54
  Length = 2.54
  Width = 2.54
FEATURE [Part::Chamfer] Chamfer042  label="Chamfer050"
  Base = -> Box269
  Edges = 4 edges r=0.5: [Edge2,Edge4,Edge6,Edge8]
FEATURE [Part::Box] Box270  label="Cube247"
  AttacherType = Attacher::AttachEngine3D
  Height = 2.54
  Length = 2.54
  Width = 2.54
FEATURE [Part::Chamfer] Chamfer061  label="Chamfer078"
  Base = -> Box270
  Edges = 4 edges r=0.5: [Edge2,Edge4,Edge6,Edge8]
FEATURE [Part::Box] Box271  label="Cube248"
  AttacherType = Attacher::AttachEngine3D
  Height = 1
  Length = 1
  Placement = pos=(0.77,-5,0.77) rot=(0,0,1;0rad)
  Width = 10
FEATURE [Part::Box] Box272  label="Cube249"
  AttacherType = Attacher::AttachEngine3D
  Height = 2.54
  Length = 2.54
  Width = 2.54
FEATURE [Part::Chamfer] Chamfer055  label="Chamfer072"
  Base = -> Box272
  Edges = 4 edges r=0.5: [Edge2,Edge4,Edge6,Edge8]
FEATURE [Part::Box] Box273  label="Cube250"
  AttacherType = Attacher::AttachEngine3D
  Height = 2.54
  Length = 2.54
  Width = 2.54
FEATURE [Part::Chamfer] Chamfer036  label="Chamfer053"
  Base = -> Box273
  Edges = 4 edges r=0.5: [Edge2,Edge4,Edge6,Edge8]
FEATURE [Part::Box] Box274  label="Cube251"
  AttacherType = Attacher::AttachEngine3D
  Height = 2.54
  Length = 2.54
  Width = 2.54
FEATURE [Part::Chamfer] Chamfer059  label="Chamfer076"
  Base = -> Box274
  Edges = 4 edges r=0.5: [Edge2,Edge4,Edge6,Edge8]
FEATURE [Part::Box] Box275  label="Cube252"
  AttacherType = Attacher::AttachEngine3D
  Height = 1
  Length = 1
  Placement = pos=(0.77,-5,0.77) rot=(0,0,1;0rad)
  Width = 10
FEATURE [Part::Box] Box276  label="Cube253"
  AttacherType = Attacher::AttachEngine3D
  Height = 2.54
  Length = 2.54
  Width = 2.54
FEATURE [Part::Chamfer] Chamfer040  label="Chamfer052"
  Base = -> Box276
  Edges = 4 edges r=0.5: [Edge2,Edge4,Edge6,Edge8]
FEATURE [Part::Box] Box277  label="Cube254"
  AttacherType = Attacher::AttachEngine3D
  Height = 2.54
  Length = 2.54
  Width = 2.54
FEATURE [Part::Chamfer] Chamfer052  label="Chamfer069"
  Base = -> Box277
  Edges = 4 edges r=0.5: [Edge2,Edge4,Edge6,Edge8]
FEATURE [Part::Box] Box278  label="Cube255"
  AttacherType = Attacher::AttachEngine3D
  Height = 2.54
  Length = 2.54
  Width = 2.54
FEATURE [Part::Chamfer] Chamfer057  label="Chamfer074"
  Base = -> Box278
  Edges = 4 edges r=0.5: [Edge2,Edge4,Edge6,Edge8]
FEATURE [Part::Box] Box279  label="Cube256"
  AttacherType = Attacher::AttachEngine3D
  Height = 2.54
  Length = 2.54
  Width = 2.54
FEATURE [Part::Chamfer] Chamfer058  label="Chamfer075"
  Base = -> Box279
  Edges = 4 edges r=0.5: [Edge2,Edge4,Edge6,Edge8]
FEATURE [Part::Box] Box280  label="Cube257"
  AttacherType = Attacher::AttachEngine3D
  Height = 2.54
  Length = 2.54
  Width = 2.54
FEATURE [Part::Chamfer] Chamfer054  label="Chamfer071"
  Base = -> Box280
  Edges = 4 edges r=0.5: [Edge2,Edge4,Edge6,Edge8]
FEATURE [Part::Box] Box281  label="Cube258"
  AttacherType = Attacher::AttachEngine3D
  Height = 1
  Length = 1
  Placement = pos=(0.77,-5,0.77) rot=(0,0,1;0rad)
  Width = 10
FEATURE [Part::Box] Box282  label="Cube259"
  AttacherType = Attacher::AttachEngine3D
  Height = 1
  Length = 1
  Placement = pos=(0.77,-5,0.77) rot=(0,0,1;0rad)
  Width = 10
FEATURE [Part::Box] Box283  label="Cube260"
  AttacherType = Attacher::AttachEngine3D
  Height = 1
  Length = 1
  Placement = pos=(0.77,-5,0.77) rot=(0,0,1;0rad)
  Width = 10
FEATURE [Part::Box] Box284  label="Cube261"
  AttacherType = Attacher::AttachEngine3D
  Height = 11
  Length = 2.54
  Placement = pos=(-1.27,-8.3,2) rot=(0,0,1;0rad)
  Width = 2.54
FEATURE [Part::Box] Box285  label="Cube262"
  AttacherType = Attacher::AttachEngine3D
  Height = 2.54
  Length = 2.54
  Width = 2.54
FEATURE [Part::Chamfer] Chamfer060  label="Chamfer077"
  Base = -> Box285
  Edges = 4 edges r=0.5: [Edge2,Edge4,Edge6,Edge8]
FEATURE [Part::Box] Box286  label="Cube263"
  AttacherType = Attacher::AttachEngine3D
  Height = 2.54
  Length = 2.54
  Width = 2.54
FEATURE [Part::Chamfer] Chamfer056  label="Chamfer073"
  Base = -> Box286
  Edges = 4 edges r=0.5: [Edge2,Edge4,Edge6,Edge8]
FEATURE [Part::MultiFuse] Fusion065  label="pcb cutouts001"
  Shapes = -> [Fusion064,Cylinder382,Cylinder358,Cylinder383,Cylinder384,Cylinder360]
FEATURE [Part::Cut] Cut194  label="PCB006"
  Base = -> Box236
  Tool = -> Fusion065
FEATURE [Part::Feature] Part__Feature432  label="Chamfer079"
  shape: bbox 2.54 x 2.54 x 2.54 mm, 22 faces (baked)
FEATURE [Part::Feature] Part__Feature433  label="Chamfer080"
  shape: bbox 2.54 x 2.54 x 2.54 mm, 22 faces (baked)
FEATURE [Part::Feature] Part__Feature434  label="Fillet036"
  shape: bbox 7.5 x 0.64 x 7.3 mm, 18 faces (baked)
FEATURE [Part::Feature] Part__Feature435  label="Antenna003"
  Placement = pos=(-16,-5,15) rot=(0.57735,0.57735,0.57735;4.18879rad)
  shape: bbox 16.04 x 7.828 x 6.038 mm, 26 faces (baked)
FEATURE [Part::Feature] Part__Feature436  label="Chamfer081"
  shape: bbox 2.54 x 2.54 x 2.54 mm, 22 faces (baked)
FEATURE [Part::Feature] Part__Feature437  label="GPS_connector001"
  Placement = pos=(-0.2977,1.3,-0.303869) rot=(-1,0,0;1.5708rad)
  shape: bbox 5.25 x 2.059 x 3.5 mm, 38 faces (baked)
FEATURE [Part::Feature] Part__Feature438  label="Chamfer082"
  shape: bbox 2.54 x 2.54 x 2.54 mm, 22 faces (baked)
FEATURE [Part::Feature] Part__Feature439  label="Chamfer083"
  shape: bbox 2.54 x 2.54 x 2.54 mm, 22 faces (baked)
FEATURE [Part::Feature] Part__Feature440  label="Fillet037"
  shape: bbox 7.5 x 0.64 x 7.3 mm, 18 faces (baked)
FEATURE [Part::Compound] Compound138  label="bent pin016"
  Links = -> [Part__Feature439,Part__Feature440]
  Placement = pos=(0,0,17.78) rot=(-1,0,0;1.5708rad)
FEATURE [Part::Feature] Part__Feature441  label="Fillet038"
  shape: bbox 7.5 x 0.64 x 7.3 mm, 18 faces (baked)
FEATURE [Part::Feature] Part__Feature442  label="Fillet039"
  Placement = pos=(0,0,0) rot=(1,0,0;1.5708rad)
  shape: bbox 7.5 x 7.3 x 0.64 mm, 18 faces (baked)
FEATURE [Part::Feature] Part__Feature443  label="Fillet040"
  shape: bbox 7.5 x 0.64 x 7.3 mm, 18 faces (baked)
FEATURE [Part::Compound] Compound135  label="bent pin014"
  Links = -> [Part__Feature436,Part__Feature443]
  Placement = pos=(0,0,7.62) rot=(-1,0,0;1.5708rad)
FEATURE [Part::Feature] Part__Feature444  label="Chamfer051"
  shape: bbox 2.54 x 2.54 x 2.54 mm, 22 faces (baked)
FEATURE [Part::Compound] Compound134  label="bent pin013"
  Links = -> [Part__Feature444,Part__Feature441]
  Placement = pos=(0,0,12.7) rot=(-1,0,0;1.5708rad)
FEATURE [Part::Feature] Part__Feature445  label="Fillet041"
  Placement = pos=(0,0,0) rot=(1,0,0;1.5708rad)
  shape: bbox 7.5 x 7.3 x 0.64 mm, 18 faces (baked)
FEATURE [Part::Feature] Part__Feature446  label="Chamfer057"
  shape: bbox 2.54 x 2.54 x 2.54 mm, 22 faces (baked)
FEATURE [Part::Feature] Part__Feature447  label="Antenna_connector001"
  Placement = pos=(1.97581,1.55,13.0153) rot=(-0.997842,-0.046433,-0.046433;1.57296rad)
  shape: bbox 4.331 x 2.3 x 9.572 mm, 71 faces (baked)
FEATURE [Part::Compound] Compound154  label="meo6mv003"
  Links = -> [Part__Feature435,Cut191,Cut188,Part__Feature447,Part__Feature430,Part__Feature425,Part__Feature426,Part__Feature424,Part__Feature428,Part__Feature429,Part__Feature437,Fillet030,Part__Feature427,Cut194,Cut193,Cut185,Part__Feature431,Cut186,Cut184]
  Placement = pos=(10,-9.3,54.5) rot=(0,0,1;0rad)
FEATURE [Part::Feature] Part__Feature448  label="Fillet042"
  shape: bbox 7.5 x 0.64 x 7.3 mm, 18 faces (baked)
FEATURE [Part::Compound] Compound140  label="bent pin017"
  Links = -> [Part__Feature433,Part__Feature448]
  Placement = pos=(0,0,0) rot=(-1,0,0;1.5708rad)
FEATURE [Part::Feature] Part__Feature449  label="Fillet043"
  shape: bbox 7.5 x 0.64 x 7.3 mm, 18 faces (baked)
FEATURE [Part::Compound] Compound146  label="bent pin018"
  Links = -> [Part__Feature438,Part__Feature449]
  Placement = pos=(0,0,2.54) rot=(-1,0,0;1.5708rad)
FEATURE [Part::Feature] Part__Feature450  label="Chamfer058"
  Placement = pos=(0,0,0) rot=(1,0,0;1.5708rad)
  shape: bbox 2.54 x 2.54 x 2.54 mm, 22 faces (baked)
FEATURE [Part::Feature] Part__Feature451  label="Fillet044"
  Placement = pos=(0,0,0) rot=(1,0,0;1.5708rad)
  shape: bbox 7.5 x 7.3 x 0.64 mm, 18 faces (baked)
FEATURE [Part::Feature] Part__Feature452  label="Chamfer059"
  Placement = pos=(0,0,0) rot=(1,0,0;1.5708rad)
  shape: bbox 2.54 x 2.54 x 2.54 mm, 22 faces (baked)
FEATURE [Part::Feature] Part__Feature453  label="Fillet045"
  shape: bbox 7.5 x 0.64 x 7.3 mm, 18 faces (baked)
FEATURE [Part::Compound] Compound148  label="bent pin019"
  Links = -> [Part__Feature432,Part__Feature453]
  Placement = pos=(0,0,5.08) rot=(-1,0,0;1.5708rad)
FEATURE [Part::Feature] Part__Feature454  label="Fillet046"
  shape: bbox 7.5 x 0.64 x 7.3 mm, 18 faces (baked)
FEATURE [Part::Compound] Compound137  label="bent pin015"
  Links = -> [Part__Feature446,Part__Feature454]
  Placement = pos=(0,0,15.24) rot=(-1,0,0;1.5708rad)
FEATURE [Part::Feature] Part__Feature455  label="Chamfer084"
  shape: bbox 2.54 x 2.54 x 2.54 mm, 22 faces (baked)
FEATURE [Part::Compound] Compound133  label="bent pin012"
  Links = -> [Part__Feature455,Part__Feature434]
  Placement = pos=(0,0,10.16) rot=(-1,0,0;1.5708rad)
FEATURE [Part::Compound] Compound139  label="pins ESP32 002"
  Links = -> [Compound148,Compound134,Compound137,Compound138,Compound146,Compound133,Compound135,Compound140]
  Placement = pos=(-8.83,0.6,48.73) rot=(0,0,1;0rad)
FEATURE [Part::Feature] Part__Feature456  label="Chamfer085"
  Placement = pos=(0,0,0) rot=(1,0,0;1.5708rad)
  shape: bbox 2.54 x 2.54 x 2.54 mm, 22 faces (baked)
FEATURE [Part::Feature] Part__Feature457  label="Fillet047"
  Placement = pos=(0,0,0) rot=(1,0,0;1.5708rad)
  shape: bbox 7.5 x 7.3 x 0.64 mm, 18 faces (baked)
FEATURE [Part::Compound] Compound157  label="bent pin021"
  Links = -> [Part__Feature450,Part__Feature451]
  Placement = pos=(0,0,0) rot=(0,-1,0;1.5708rad)
FEATURE [Part::Compound] Compound156  label="bent pin + connector004"
  Links = -> [Compound157,Box245]
FEATURE [Part::Compound] Compound159  label="straight pin + connector023"
  Links = -> [Box275,Chamfer036]
  Placement = pos=(0,0,17.78) rot=(0,0,1;0rad)
FEATURE [Part::Compound] Compound160  label="straight pin + connector024"
  Links = -> [Chamfer039]
  Placement = pos=(0,0,2.54) rot=(0,0,1;0rad)
FEATURE [Part::Compound] Compound161  label="straight pin + connector025"
  Links = -> [Chamfer040]
FEATURE [Part::Compound] Compound162  label="straight pin + connector026"
  Links = -> [Chamfer054]
  Placement = pos=(0,0,7.62) rot=(0,0,1;0rad)
FEATURE [Part::Compound] Compound164  label="straight pin008"
  Links = -> [Box266,Chamfer057]
  Placement = pos=(0,0,15.24) rot=(0,0,1;0rad)
FEATURE [Part::Compound] Compound165  label="straight pin + connector027"
  Links = -> [Chamfer058]
FEATURE [Part::Compound] Compound166  label="straight pin + connector028"
  Links = -> [Chamfer052]
  Placement = pos=(0,0,17.78) rot=(0,0,1;0rad)
FEATURE [Part::Compound] Compound168  label="straight pin + connector029"
  Links = -> [Box282,Chamfer050]
  Placement = pos=(0,0,10.16) rot=(0,0,1;0rad)
FEATURE [Part::Compound] Compound169  label="straight pin009"
  Links = -> [Box281,Chamfer059]
  Placement = pos=(0,0,15.24) rot=(0,0,1;0rad)
FEATURE [Part::Compound] Compound170  label="straight pin010"
  Links = -> [Box263,Chamfer053]
  Placement = pos=(0,0,12.7) rot=(0,0,1;0rad)
FEATURE [Part::Compound] Compound172  label="straight pin011"
  Links = -> [Chamfer051]
  Placement = pos=(0,0,12.7) rot=(0,0,1;0rad)
FEATURE [Part::Compound] Compound174  label="bent pin022"
  Links = -> [Part__Feature452,Part__Feature445]
  Placement = pos=(0,0,0) rot=(0,-1,0;1.5708rad)
FEATURE [Part::Compound] Compound173  label="bent pin + connector007"
  Links = -> [Compound174,Box249]
  Placement = pos=(2.54,0,0) rot=(0,0,1;0rad)
FEATURE [Part::Compound] Compound175  label="bent pin023"
  Links = -> [Part__Feature456,Part__Feature442]
  Placement = pos=(0,0,0) rot=(0,-1,0;1.5708rad)
FEATURE [Part::Compound] Compound163  label="bent pin + connector005"
  Links = -> [Compound175,Box262]
  Placement = pos=(5.08,0,0) rot=(0,0,1;0rad)
FEATURE [Part::Compound] Compound176  label="straight pin + connector030"
  Links = -> [Chamfer042]
  Placement = pos=(0,0,10.16) rot=(0,0,1;0rad)
FEATURE [Part::Compound] Compound177  label="straight pin 004"
  Links = -> [Chamfer055]
  Placement = pos=(0,0,5.08) rot=(0,0,1;0rad)
FEATURE [Part::Compound] Compound171  label="pins ESP32cam 003"
  Links = -> [Compound161,Compound159,Compound162,Compound172,Compound176,Compound160,Compound177,Compound164]
  Placement = pos=(10.9,10.5,51.2) rot=(0,0,1;0rad)
FEATURE [Part::Feature] Part__Feature458  label="Chamfer056"
  Placement = pos=(0,0,0) rot=(1,0,0;1.5708rad)
  shape: bbox 2.54 x 2.54 x 2.54 mm, 22 faces (baked)
FEATURE [Part::Compound] Compound155  label="bent pin020"
  Links = -> [Part__Feature458,Part__Feature457]
  Placement = pos=(0,0,0) rot=(0,-1,0;1.5708rad)
FEATURE [Part::Compound] Compound167  label="bent pin + connector006"
  Links = -> [Compound155,Box284]
  Placement = pos=(7.62,0,0) rot=(0,0,1;0rad)
FEATURE [Part::Compound] Compound158  label="pins GPS001"
  Links = -> [Compound156,Compound167,Compound163,Compound173]
  Placement = pos=(-2.62,-6.4,37.5) rot=(0,0,1;0rad)
FEATURE [Part::Compound] Compound178  label="straight pin + connector031"
  Links = -> [Chamfer061]
  Placement = pos=(0,0,7.62) rot=(0,0,1;0rad)
FEATURE [Part::Compound] Compound179  label="straight pin 005"
  Links = -> [Box283,Chamfer056]
  Placement = pos=(0,0,5.08) rot=(0,0,1;0rad)
FEATURE [Part::Compound] Compound181  label="straight pin + connector032"
  Links = -> [Box271,Chamfer060]
  Placement = pos=(0,0,2.54) rot=(0,0,1;0rad)
FEATURE [Part::Compound] Compound180  label="pins ESP32cam 004"
  Links = -> [Compound165,Compound166,Compound178,Compound170,Compound168,Compound181,Compound179,Compound169]
  Placement = pos=(-12.1,10.5,51.2) rot=(0,0,1;0rad)
FEATURE [Part::Compound] Compound182  label="connectors001"
  Links = -> [Compound147,Compound139,Box260,Compound158,Compound171,Compound180]
FEATURE [Part::Compound] Compound183  label="Content (middle)"
  Links = -> [Compound182,Fillet028,Box224,Compound122,Fusion063,Compound154]
FEATURE [Part::Box] Box288  label="Cube264"
  AttacherType = Attacher::AttachEngine3D
  Height = 40
  Length = 1
  Placement = pos=(-14.4,-0.3,36) rot=(0,0,1;0rad)
  Width = 2
FEATURE [Part::Box] Box289  label="Cube265"
  AttacherType = Attacher::AttachEngine3D
  Height = 40
  Length = 1
  Placement = pos=(-14.4,3.5,36) rot=(0,0,1;0rad)
  Width = 2
FEATURE [Part::Compound] Compound184  label="ESP32minikit clamping001"
  Links = -> [Chamfer035,Chamfer032,Chamfer033,Box288,Box289]
FEATURE [Part::Box] Box290  label="Cube266"
  AttacherType = Attacher::AttachEngine3D
  Height = 11
  Length = 5
  Placement = pos=(-14.4,-6,25) rot=(0,0,1;0rad)
  Width = 17
FEATURE [Part::Box] Box291  label="Cube267"
  AttacherType = Attacher::AttachEngine3D
  Height = 7.5
  Length = 3
  Placement = pos=(-12,-6,27) rot=(0,0,1;0rad)
  Width = 17
FEATURE [Part::Cut] Cut198  label="Battery clamping"
  Base = -> Box290
  Tool = -> Box291
FEATURE [Part::Box] Box292  label="Cube268"
  AttacherType = Attacher::AttachEngine3D
  Height = 5
  Length = 5
  Placement = pos=(-14,4.5,36) rot=(0,0,1;0rad)
  Width = 3
FEATURE [Part::Chamfer] Chamfer062  label="Chamfer086"
  Base = -> Box292
  Edges = 1 edges: [Edge7 r1=2 r2=4]
  Placement = pos=(-0.4,-12,30.5) rot=(0,0,1;0rad)
FEATURE [Part::Box] Box293  label="Cube269"
  AttacherType = Attacher::AttachEngine3D
  Height = 5
  Length = 5
  Width = 3
FEATURE [Part::Box] Box294  label="Cube270"
  AttacherType = Attacher::AttachEngine3D
  Height = 5
  Length = 5
  Placement = pos=(-14,4.5,36) rot=(0,0,1;0rad)
  Width = 3
FEATURE [Part::Chamfer] Chamfer063  label="Chamfer087"
  Base = -> Box293
  Edges = 1 edges: [Edge5 r1=2 r2=4]
  Placement = pos=(-14.4,-12,35) rot=(0,0,1;0rad)
FEATURE [Part::Chamfer] Chamfer064  label="Chamfer088"
  Base = -> Box294
  Edges = 1 edges: [Edge7 r1=2 r2=4]
  Placement = pos=(-0.4,-12,-1) rot=(0,0,1;0rad)
FEATURE [Part::Box] Box295  label="Cube271"
  AttacherType = Attacher::AttachEngine3D
  Height = 35.5
  Length = 1
  Placement = pos=(-14.4,-11,36) rot=(0,0,1;0rad)
  Width = 2
FEATURE [Part::Box] Box296  label="Cube272"
  AttacherType = Attacher::AttachEngine3D
  Height = 35.5
  Length = 1
  Placement = pos=(-14.4,-7.5,36) rot=(0,0,1;0rad)
  Width = 2
FEATURE [Part::Box] Box297  label="Cube273"
  AttacherType = Attacher::AttachEngine3D
  Height = 5
  Length = 5
  Width = 3
FEATURE [Part::Chamfer] Chamfer065  label="Chamfer089"
  Base = -> Box297
  Edges = 1 edges: [Edge5 r1=2 r2=4]
  Placement = pos=(-14.4,-12,66.5) rot=(0,0,1;0rad)
FEATURE [Part::Box] Box298  label="Cube274"
  AttacherType = Attacher::AttachEngine3D
  Height = 54.9
  Length = 2
  Placement = pos=(14,-15.5,36) rot=(0,0,1;0rad)
  Width = 19
FEATURE [Part::Cut] Cut201  label="side plate001"
  Base = -> Box203
  Tool = -> Box298
FEATURE [Part::Box] Box299  label="Cube275"
  AttacherType = Attacher::AttachEngine3D
  Height = 11
  Length = 8
  Placement = pos=(6,-2,25) rot=(0,0,1;0rad)
  Width = 4
FEATURE [Part::Box] Box300  label="Cube276"
  AttacherType = Attacher::AttachEngine3D
  Height = 7.5
  Length = 5
  Placement = pos=(4,-2,27) rot=(0,0,1;0rad)
  Width = 4
FEATURE [Part::Cut] Cut202  label="battery clamping001"
  Base = -> Box299
  Tool = -> Box300
FEATURE [Part::Box] Box301  label="ESP32minikit clamping"
  AttacherType = Attacher::AttachEngine3D
  Height = 5
  Length = 5.5
  Placement = pos=(10.5,-2,36) rot=(0,0,1;0rad)
  Width = 3.7
FEATURE [Part::Cylinder] Cylinder392
  Angle = 360
  AttacherType = Attacher::AttachEngine3D
  Height = 62
  Placement = pos=(0,0,23) rot=(0,0,1;0rad)
  Radius = 21
FEATURE [Part::Cylinder] Cylinder393
  Angle = 360
  AttacherType = Attacher::AttachEngine3D
  Height = 2
  Placement = pos=(0,0,23) rot=(0,0,1;0rad)
  Radius = 22
FEATURE [Part::MultiFuse] Fusion069  label="Acceptable volume (centre)005"
  Shapes = -> [Cylinder393,Cylinder392]
FEATURE [Part::Compound] Compound186
  Links = -> [Box201,Box197]
FEATURE [Part::Cut] Cut204  label="Wide pole plate"
  Base = -> Box208
  Tool = -> Compound186
FEATURE [Part::Box] Box302  label="Cube278"
  AttacherType = Attacher::AttachEngine3D
  Height = 9
  Length = 2
  Placement = pos=(14,3.5,76) rot=(0,0,1;0rad)
  Width = 1
FEATURE [Part::Cylinder] Cylinder394
  Angle = 360
  AttacherType = Attacher::AttachEngine3D
  Height = 1
  Placement = pos=(0,0,24) rot=(0,0,1;0rad)
  Radius = 15
FEATURE [Part::Box] Box  label="Cube"
  AttacherType = Attacher::AttachEngine3D
  Height = 1
  Length = 4
  Placement = pos=(-2,-16,24) rot=(0,0,1;0rad)
  Width = 2
FEATURE [Part::Box] Box303  label="Cube279"
  AttacherType = Attacher::AttachEngine3D
  Height = 1
  Length = 5
  Placement = pos=(-14.3,-6,24) rot=(0,0,1;0rad)
  Width = 18
FEATURE [Part::Box] Box304  label="Cube280"
  AttacherType = Attacher::AttachEngine3D
  Height = 1
  Length = 3.4
  Placement = pos=(10.5,-2,24) rot=(0,0,1;0rad)
  Width = 13
FEATURE [Part::Compound] Compound189  label="build-up"
  Links = -> [Box303,Box304]
FEATURE [Part::MultiFuse] Fusion072  label="cut-outs"
  Shapes = -> [Cylinder394,Box,Cylinder227,Box195,Box196,Cylinder233,Cylinder238,Box220,Box221]
FEATURE [Part::Cut] Cut206
  Base = -> Cylinder239
  Tool = -> Fusion072
FEATURE [Part::Compound] Compound190  label="Base plate"
  Links = -> [Cut133,Cut206,Compound189]
FEATURE [Part::Box] Box305  label="Cube281"
  AttacherType = Attacher::AttachEngine3D
  Height = 35
  Length = 1
  Placement = pos=(14,3.5,36) rot=(0,0,1;0rad)
  Width = 5
FEATURE [Part::MultiFuse] Fusion073
  Shapes = -> [Box302,Box305,Box202,Cylinder237,Box213]
FEATURE [Part::Cut] Cut207
  Base = -> Cut201
  Tool = -> Fusion073
FEATURE [Part::Fillet] Fillet031  label="wall"
  Base = -> Cut207
  Edges = 2 edges r=2: [Edge35,Edge36]
FEATURE [Part::Compound] Compound191
  Links = -> [Cut129,Fillet031,Cut202,Box301]
FEATURE [Part::MultiCommon] Common  label="Narrow side pole"
  Shapes = -> [Fusion069,Compound191]
FEATURE [Part::Box] Box306  label="Cube282"
  AttacherType = Attacher::AttachEngine3D
  Height = 5
  Length = 5
  Width = 3
FEATURE [Part::Chamfer] Chamfer067  label="Chamfer091"
  Base = -> Box306
  Edges = 1 edges: [Edge5 r1=2 r2=4]
  Placement = pos=(-14.4,10,34) rot=(0,0,1;0rad)
FEATURE [Part::Box] Box307  label="Cube283"
  AttacherType = Attacher::AttachEngine3D
  Height = 3
  Length = 4
  Placement = pos=(-14,4.5,36) rot=(0,0,1;0rad)
  Width = 3
FEATURE [Part::Chamfer] Chamfer068  label="Chamfer092"
  Base = -> Box307
  Edges = 1 edges: [Edge7 r1=2 r2=3]
  Placement = pos=(-0.4,10.4,37) rot=(0,0,1;0rad)
FEATURE [Part::Box] Box308  label="Cube284"
  AttacherType = Attacher::AttachEngine3D
  Height = 5
  Length = 5
  Placement = pos=(-14,4.5,36) rot=(0,0,1;0rad)
  Width = 3
FEATURE [Part::Chamfer] Chamfer066  label="Chamfer090"
  Base = -> Box308
  Edges = 1 edges: [Edge7 r1=2 r2=4]
  Placement = pos=(-0.4,10.4,-2) rot=(0,0,1;0rad)
FEATURE [Part::Box] Box309  label="Cube285"
  AttacherType = Attacher::AttachEngine3D
  Height = 3
  Length = 4
  Width = 3
FEATURE [Part::Chamfer] Chamfer069  label="Chamfer093"
  Base = -> Box309
  Edges = 1 edges: [Edge5 r1=2 r2=3]
  Placement = pos=(-14.4,10,73) rot=(0,0,1;0rad)
FEATURE [Part::Compound] Compound192  label="NEO6MV2 clamping"
  Links = -> [Chamfer065,Chamfer064,Chamfer063,Chamfer062,Box295,Box296]
FEATURE [Part::Box] Box310  label="Cube286"
  AttacherType = Attacher::AttachEngine3D
  Height = 1
  Length = 4
  Placement = pos=(-13.4,12,34) rot=(0,0,1;0rad)
  Width = 3.9
FEATURE [Part::MultiFuse] Fusion074
  Shapes = -> [Box190,Box310,Chamfer069,Chamfer067,Chamfer068,Chamfer066]
FEATURE [Part::Cut] Cut208  label="ESP32cam clamping"
  Base = -> Fusion074
  Tool = -> Box204
FEATURE [Part::Compound] Compound193
  Links = -> [Fillet024,Cut208,Compound184,Cut198,Cut204,Compound192]
FEATURE [Part::MultiCommon] Common004  label="Wide side pole"
  Shapes = -> [Compound193,Fusion060]
FEATURE [Part::Compound] Compound194  label="Structure (middle)"
  Links = -> [Compound190,Common,Common004]
FEATURE [Part::Box] Box311  label="Cube287"
  AttacherType = Attacher::AttachEngine3D
  Height = 2.54
  Length = 2.54
  Width = 2.54
FEATURE [Part::Chamfer] Chamfer071  label="Chamfer095"
  Base = -> Box311
  Edges = 4 edges r=0.5: [Edge2,Edge4,Edge6,Edge8]
FEATURE [Part::Box] Box312  label="Cube288"
  AttacherType = Attacher::AttachEngine3D
  Height = 1
  Length = 1
  Placement = pos=(0.77,-5,0.77) rot=(0,0,1;0rad)
  Width = 10
FEATURE [Part::Compound] Compound195  label="straight pin012"
  Links = -> [Box312,Chamfer071]
  Placement = pos=(0,0,0) rot=(0,0,1;1.5708rad)
FEATURE [Part::Box] Box313  label="Cube289"
  AttacherType = Attacher::AttachEngine3D
  Height = 1
  Length = 1
  Placement = pos=(0.77,-5,0.77) rot=(0,0,1;0rad)
  Width = 10
FEATURE [Part::Box] Box314  label="Cube290"
  AttacherType = Attacher::AttachEngine3D
  Height = 2.54
  Length = 2.54
  Width = 2.54
FEATURE [Part::Chamfer] Chamfer070  label="Chamfer094"
  Base = -> Box314
  Edges = 4 edges r=0.5: [Edge2,Edge4,Edge6,Edge8]
FEATURE [Part::Compound] Compound196  label="straight pin 006"
  Links = -> [Box313,Chamfer070]
  Placement = pos=(0,2.54,0) rot=(0,0,1;1.5708rad)
FEATURE [Part::Compound] Compound197  label="on/off header"
  Links = -> [Compound195,Compound196]
  Placement = pos=(16,-2.5,20) rot=(0,0,1;0rad)
FEATURE [Part::Box] Box315  label="cut-out on-off jumper"
  AttacherType = Attacher::AttachEngine3D
  Height = 3
  Length = 13
  Placement = pos=(10,-2.5,21) rot=(0,0,1;0rad)
  Width = 5.1
FEATURE [Part::Compound] Compound199  label="Content (bottom)"
  Links = -> [Prism021,Compound,Compound042,Compound041,Compound040,Part__Feature294,Prism019,Prism020,Compound197]
FEATURE [Part::Box] Box316  label="Cube292"
  AttacherType = Attacher::AttachEngine3D
  Height = 9
  Length = 3
  Placement = pos=(-17.5,-4.6,76) rot=(0,0,1;0rad)
  Width = 2
FEATURE [Part::Cylinder] Cylinder395
  Angle = 360
  AttacherType = Attacher::AttachEngine3D
  Height = 5
  Placement = pos=(-5.8,-6,95.9) rot=(1,0,0;1.5708rad)
  Radius = 1.5
FEATURE [Part::Box] Box317  label="Cube293"
  AttacherType = Attacher::AttachEngine3D
  Height = 17
  Length = 7
  Placement = pos=(-3.5,-4.6,103) rot=(0,0,1;0rad)
  Width = 2
FEATURE [Part::Cylinder] Cylinder396
  Angle = 360
  AttacherType = Attacher::AttachEngine3D
  Height = 10
  Placement = pos=(0,0,120) rot=(0,0,1;0rad)
  Radius = 1.7
FEATURE [Part::Cylinder] Cylinder397
  Angle = 360
  AttacherType = Attacher::AttachEngine3D
  Height = 5
  Placement = pos=(8,0,100.8) rot=(1,0,0;1.5708rad)
  Radius = 1.5
FEATURE [Part::Cylinder] Cylinder398
  Angle = 360
  AttacherType = Attacher::AttachEngine3D
  Height = 5
  Placement = pos=(5.2,-6,95.9) rot=(1,0,0;1.5708rad)
  Radius = 1.5
FEATURE [Part::Cylinder] Cylinder399
  Angle = 360
  AttacherType = Attacher::AttachEngine3D
  Height = 9
  Placement = pos=(0,0,76) rot=(0,0,1;0rad)
  Radius = 21
FEATURE [Part::Box] Box319  label="Cut-out narrow pole"
  AttacherType = Attacher::AttachEngine3D
  Height = 2
  Length = 2.4
  Placement = pos=(13.9,4.3,76) rot=(0,0,1;0rad)
  Width = 6.4
FEATURE [Part::Cylinder] Cylinder400
  Angle = 360
  AttacherType = Attacher::AttachEngine3D
  Height = 3
  Placement = pos=(0,0,123) rot=(0,0,1;0rad)
  Radius = 4
FEATURE [Part::Prism] Prism028
  AttacherType = Attacher::AttachEngine3D
  Circumradius = 3.3
  Height = 2.4
  Placement = pos=(0,0,123.6) rot=(0,0,1;0rad)
  Polygon = 6
FEATURE [Part::MultiFuse] Fusion076  label="Fusion075"
  Shapes = -> [Prism028,Cylinder396]
FEATURE [Part::Cylinder] Cylinder401
  Angle = 360
  AttacherType = Attacher::AttachEngine3D
  Height = 5
  Placement = pos=(-8,0,100.8) rot=(1,0,0;1.5708rad)
  Radius = 1.5
FEATURE [Part::Box] Box320  label="Cut-out wide pole"
  AttacherType = Attacher::AttachEngine3D
  Height = 2
  Length = 2.2
  Placement = pos=(-16.7,-4.2,76) rot=(0,0,1;0rad)
  Width = 10.4
FEATURE [Part::Box] Box322  label="Cube298"
  AttacherType = Attacher::AttachEngine3D
  Height = 22
  Length = 24
  Placement = pos=(-12,-4.6,76) rot=(0,0,1;0rad)
  Width = 6
FEATURE [Part::Cylinder] Cylinder402
  Angle = 360
  AttacherType = Attacher::AttachEngine3D
  Height = 3
  Placement = pos=(0,0,120) rot=(0,0,1;0rad)
  Radius = 8
FEATURE [Part::Box] Box324  label="Base"
  AttacherType = Attacher::AttachEngine3D
  Height = 44
  Length = 34
  Placement = pos=(-17,-4.6,76) rot=(0,0,1;0rad)
  Width = 2
FEATURE [Part::Cone] Cone004  label="Cone005"
  Angle = 360
  AttacherType = Attacher::AttachEngine3D
  Height = 41
  Placement = pos=(0,0,85) rot=(0,0,1;0rad)
  Radius1 = 21
  Radius2 = 5
FEATURE [Part::MultiFuse] Fusion077  label="acceptable volume (top)001"
  Shapes = -> [Cylinder399,Cone004]
FEATURE [Part::MultiFuse] Fusion078  label="Fusion083"
  Shapes = -> [Cylinder400,Cylinder402]
FEATURE [Part::Cut] Cut210  label="Cut224"
  Base = -> Fusion078
  Tool = -> Fusion076
FEATURE [Part::Cylinder] Cylinder403
  Angle = 360
  AttacherType = Attacher::AttachEngine3D
  Height = 10
  Placement = pos=(-20,1,72) rot=(0,1,0;1.5708rad)
  Radius = 1.5
FEATURE [Part::Cylinder] Cylinder404
  Angle = 360
  AttacherType = Attacher::AttachEngine3D
  Height = 10
  Placement = pos=(10,7.75,72) rot=(0,1,0;1.5708rad)
  Radius = 1.5
FEATURE [Part::Cylinder] Cylinder405  label="Base plate001"
  Angle = 360
  AttacherType = Attacher::AttachEngine3D
  Height = 2
  Placement = pos=(0,0,76) rot=(0,0,1;0rad)
  Radius = 21
FEATURE [Part::Box] Box326  label="Main cut-out 1"
  AttacherType = Attacher::AttachEngine3D
  Height = 2
  Length = 22.5
  Placement = pos=(-11.5,-12,76) rot=(0,0,1;0rad)
  Width = 16.5
FEATURE [Part::Box] Box327  label="Main cut-out 2"
  AttacherType = Attacher::AttachEngine3D
  Height = 2
  Length = 15
  Placement = pos=(-8,4.5,76) rot=(0,0,1;0rad)
  Width = 12.5
FEATURE [Part::Box] Box328  label="Cube304"
  AttacherType = Attacher::AttachEngine3D
  Height = 14
  Length = 3
  Placement = pos=(12,4.5,67) rot=(0,0,1;0rad)
  Width = 9
FEATURE [Part::Cut] Cut213
  Base = -> Box328
  Placement = pos=(-1,0,9) rot=(0,0,1;0rad)
  Tool = -> Cylinder404
FEATURE [Part::Box] Box329  label="Cube305"
  AttacherType = Attacher::AttachEngine3D
  Height = 9
  Length = 2.5
  Placement = pos=(-14.5,-4.6,67) rot=(0,0,1;0rad)
  Width = 9
FEATURE [Part::Compound] Compound200  label="Screwholes002"
  Links = -> [Cylinder397,Cylinder401]
FEATURE [Part::Compound] Compound201  label="Screwholes003"
  Links = -> [Cylinder395,Cylinder398]
FEATURE [Part::Cut] Cut223  label="fixation 004"
  Base = -> Box329
  Placement = pos=(0,0,9) rot=(0,0,1;0rad)
  Tool = -> Cylinder403
FEATURE [Part::Cylinder] Cylinder406
  Angle = 360
  AttacherType = Attacher::AttachEngine3D
  Height = 17
  Placement = pos=(0,0,103) rot=(0,0,1;0rad)
  Radius = 13
FEATURE [Part::Box] Box330  label="Cube306"
  AttacherType = Attacher::AttachEngine3D
  Height = 20
  Length = 26
  Placement = pos=(-13,-14.6,101) rot=(0,0,1;0rad)
  Width = 12
FEATURE [Part::Cylinder] Cylinder407
  Angle = 360
  AttacherType = Attacher::AttachEngine3D
  Height = 17
  Placement = pos=(0,0,103) rot=(0,0,1;0rad)
  Radius = 4.35
FEATURE [Part::Cut] Cut220  label="Cut221"
  Base = -> Cylinder406
  Tool = -> Cylinder407
FEATURE [Part::Box] Box331  label="Cube307"
  AttacherType = Attacher::AttachEngine3D
  Height = 25
  Length = 26
  Placement = pos=(-13,-3,101) rot=(-1,0,0;0.314159rad)
  Width = 15
FEATURE [Part::Cut] Cut221  label="Cut216"
  Base = -> Cut220
  Tool = -> Box331
FEATURE [Part::Cut] Cut216  label="Antenna support carrier"
  Base = -> Cut221
  Tool = -> Box330
FEATURE [Part::Box] Box338  label="cut-out connector MPU6050"
  AttacherType = Attacher::AttachEngine3D
  Height = 2
  Length = 4
  Placement = pos=(7,4.5,76) rot=(0,0,1;0rad)
  Width = 3
FEATURE [Part::Cone] Cone005  label="Cone006"
  Angle = 360
  AttacherType = Attacher::AttachEngine3D
  Height = 41
  Placement = pos=(0,0,85) rot=(0,0,1;0rad)
  Radius1 = 21
  Radius2 = 5
FEATURE [Part::MultiCommon] Common005  label="Support Antenna"
  Shapes = -> [Cut210,Cone005]
FEATURE [Part::Box] Box339  label="Cut-out leg 1"
  AttacherType = Attacher::AttachEngine3D
  Height = 2
  Length = 2.7
  Placement = pos=(-14.6,-4.7,76) rot=(0,0,1;0rad)
  Width = 11.8
FEATURE [Part::Box] Box340  label="Cut-out leg 2"
  AttacherType = Attacher::AttachEngine3D
  Height = 2
  Length = 5.2
  Placement = pos=(11.9,-4.7,76) rot=(0,0,1;0rad)
  Width = 2.2
FEATURE [Part::Chamfer] Chamfer
  Base = -> Box322
  Edges = 2 edges: [Edge2 r1=8 r2=3,Edge6 r1=8 r2=3]
FEATURE [Part::MultiFuse] Fusion085  label="cut-outs001"
  Shapes = -> [Chamfer,Box317,Compound200,Box316]
FEATURE [Part::Cut] Cut225
  Base = -> Box324
  Tool = -> Fusion085
FEATURE [Part::MultiFuse] Fusion086  label="Fusion087"
  Shapes = -> [Cut225,Cut216,Cut223]
FEATURE [Part::MultiCommon] Common006  label="Support MPU6050"
  Shapes = -> [Fusion086,Fusion077]
FEATURE [Part::Box] Box341  label="Cube314"
  AttacherType = Attacher::AttachEngine3D
  Height = 6
  Length = 22
  Placement = pos=(-11,-8,93) rot=(0,0,1;0rad)
  Width = 4
FEATURE [Part::Box] Box342  label="Cube315"
  AttacherType = Attacher::AttachEngine3D
  Height = 5
  Length = 30
  Placement = pos=(-15,-10,93) rot=(0,1,0;0rad)
  Width = 5.4
FEATURE [Part::Chamfer] Chamfer073  label="Chamfer096"
  Base = -> Box341
  Edges = 2 edges: [Edge2 r1=5.9 r2=2.4,Edge6 r1=5.9 r2=2.4]
FEATURE [Part::Chamfer] Chamfer074  label="Chamfer097"
  Base = -> Box342
  Edges = 2 edges: [Edge2 r1=3 r2=2,Edge6 r1=3 r2=2]
FEATURE [Part::MultiFuse] Fusion087  label="cut-out001"
  Shapes = -> [Compound201,Chamfer073]
FEATURE [Part::Cut] Cut226
  Base = -> Chamfer074
  Tool = -> Fusion087
FEATURE [Part::Cone] Cone007  label="Cone008"
  Angle = 360
  AttacherType = Attacher::AttachEngine3D
  Height = 41
  Placement = pos=(0,0,85) rot=(0,0,1;0rad)
  Radius1 = 21
  Radius2 = 5
FEATURE [Part::MultiCommon] Common007  label="Support BMP280"
  Shapes = -> [Cut226,Cone007]
FEATURE [Part::Box] Box343  label="Cube316"
  AttacherType = Attacher::AttachEngine3D
  Height = 13.7
  Length = 17.7
  Placement = pos=(-0.1,0,-0.1) rot=(0,0,1;0rad)
  Width = 1
FEATURE [Part::Box] Box344  label="Cube317"
  AttacherType = Attacher::AttachEngine3D
  Height = 17.5
  Length = 22
  Placement = pos=(-2,-1.5,-2) rot=(0,0,1;0rad)
  Width = 2.5
FEATURE [Part::Box] Box345  label="Cube318"
  AttacherType = Attacher::AttachEngine3D
  Height = 15.5
  Length = 13.5
  Placement = pos=(2,-1.5,-2) rot=(0,0,1;0rad)
  Width = 2.5
FEATURE [Part::Box] Box346  label="Cube319"
  AttacherType = Attacher::AttachEngine3D
  Height = 3
  Length = 3
  Placement = pos=(14.6,-1.5,10.6) rot=(0,0,1;0rad)
  Width = 2.5
FEATURE [Part::MultiFuse] Fusion088
  Shapes = -> [Box345,Box346,Box343]
FEATURE [Part::Cut] Cut227
  Base = -> Box344
  Placement = pos=(-9,6,87) rot=(0,0,1;0rad)
  Tool = -> Fusion088
FEATURE [Part::Chamfer] Chamfer075  label="Chamfer098"
  Base = -> Cut213
  Edges = 2 edges: [Edge9 r1=6.5 r2=12,Edge10 r=2.9]
FEATURE [Part::Box] Box347  label="Cube320"
  AttacherType = Attacher::AttachEngine3D
  Height = 7
  Length = 7.5
  Placement = pos=(-14.5,4.5,78) rot=(0,0,1;0rad)
  Width = 2.5
FEATURE [Part::Chamfer] Chamfer076  label="Chamfer099"
  Base = -> Box347
  Edges = 1 edges: [Edge8 r1=6.9 r2=5]
FEATURE [Part::Box] Box348  label="Cube321"
  AttacherType = Attacher::AttachEngine3D
  Height = 2
  Length = 2.5
  Placement = pos=(-14.5,4.5,76) rot=(0,0,1;0rad)
  Width = 2.5
FEATURE [Part::MultiFuse] Fusion089  label="Support WL102-341"
  Shapes = -> [Cut227,Chamfer075,Chamfer076,Box348]
FEATURE [Part::Box] Box349  label="Cut-out leg 3"
  AttacherType = Attacher::AttachEngine3D
  Height = 2
  Length = 3.2
  Placement = pos=(10.9,4.4,76) rot=(0,0,1;0rad)
  Width = 9.2
FEATURE [Part::MultiFuse] Fusion090  label="cut-outs002"
  Shapes = -> [Box320,Box326,Box327,Box319,Box349,Box340,Box339,Box338]
FEATURE [Part::Cut] Cut228  label="Baseplate"
  Base = -> Cylinder405
  Tool = -> Fusion090
FEATURE [Part::Compound] Compound202  label="Structure (top)"
  Links = -> [Common005,Common006,Common007,Fusion089,Cut228]
FEATURE [Part::Box] Box350  label="Cube322"
  AttacherType = Attacher::AttachEngine3D
  Height = 16
  Length = 33
  Placement = pos=(-16.5,-1.5,1) rot=(0,0,1;0rad)
  Width = 3
FEATURE [Part::Box] Box351  label="cut-out on-off jumper001"
  AttacherType = Attacher::AttachEngine3D
  Height = 6
  Length = 6
  Placement = pos=(10.5,-2.5,16) rot=(0,0,1;0rad)
  Width = 5.1
FEATURE [Part::MultiFuse] Fusion075  label="cut-out"
  Placement = pos=(0,0,1) rot=(0,0,1;0rad)
  Shapes = -> [Fusion016,Box315,Fusion017,Fusion014,Box058,Fusion018,Box351]
FEATURE [Part::Cut] Cut209  label="Transition cone"
  Base = -> Cone
  Tool = -> Fusion075
FEATURE [Part::Cylinder] Cylinder408
  Angle = 360
  AttacherType = Attacher::AttachEngine3D
  Height = 10
  Placement = pos=(-9,5,9) rot=(1,0,0;1.5708rad)
  Radius = 2
FEATURE [Part::Cut] Cut229
  Base = -> Box350
  Tool = -> Cylinder408
FEATURE [Part::MultiFuse] Fusion
  Shapes = -> [Cut,Cylinder224,Box189,Cut229]
FEATURE [Part::Cut] Cut230  label="Rocket interface"
  Base = -> Fusion
  Tool = -> Cylinder001
FEATURE [Part::Compound] Compound203  label="Structure (bottom)"
  Links = -> [Cut209,Cut230]
FEATURE [Part::Cone] Cone008  label="Cone009"
  Angle = 360
  AttacherType = Attacher::AttachEngine3D
  Height = 41
  Placement = pos=(0,0,75) rot=(0,0,1;0rad)
  Radius1 = 22.2
  Radius2 = 6
FEATURE [Part::Sphere] Sphere001
  Angle1 = 19
  Angle2 = 90
  Angle3 = 360
  AttacherType = Attacher::AttachEngine3D
  Placement = pos=(0,0,120.5) rot=(0,0,1;0rad)
  Radius = 7.6
FEATURE [Part::Cone] Cone009  label="Cone010"
  Angle = 360
  AttacherType = Attacher::AttachEngine3D
  Height = 41
  Placement = pos=(0,0,75) rot=(0,0,1;0rad)
  Radius1 = 21.5
  Radius2 = 5.3
FEATURE [Part::Cylinder] Cylinder409
  Angle = 360
  AttacherType = Attacher::AttachEngine3D
  Height = 3
  Placement = pos=(0,0,123) rot=(0,0,1;0rad)
  Radius = 8
FEATURE [Part::Cylinder] Cylinder411
  Angle = 360
  AttacherType = Attacher::AttachEngine3D
  Height = 4
  Placement = pos=(0,0,123) rot=(0,0,1;0rad)
  Radius = 9
FEATURE [Part::Cylinder] Cylinder412
  Angle = 360
  AttacherType = Attacher::AttachEngine3D
  Height = 63
  Radius = 22.2
FEATURE [Part::Cylinder] Cylinder413
  Angle = 360
  AttacherType = Attacher::AttachEngine3D
  Height = 63
  Radius = 21.5
FEATURE [Part::Cylinder] Cylinder414
  Angle = 360
  AttacherType = Attacher::AttachEngine3D
  Height = 10
  Placement = pos=(0.5,26,63) rot=(1,0,0;1.5708rad)
  Radius = 2.75
FEATURE [Part::Cylinder] Cylinder415
  Angle = 360
  AttacherType = Attacher::AttachEngine3D
  Height = 10
  Placement = pos=(0,0,118) rot=(0,0,1;0rad)
  Radius = 1.7
FEATURE [Part::MultiCommon] Common008
  Shapes = -> [Cylinder411,Sphere001]
FEATURE [Part::Cut] Cut233
  Base = -> Cylinder412
  Placement = pos=(0,0,22) rot=(0,0,1;0rad)
  Tool = -> Cylinder413
FEATURE [Part::Cut] Cut234  label="compound001"
  Base = -> Cone008
  Placement = pos=(0,0,10) rot=(0,0,1;0rad)
  Tool = -> Cone009
FEATURE [Part::Cut] Cut232  label="conical section001"
  Base = -> Cut234
  Tool = -> Cylinder409
FEATURE [Part::Cut] Cut235  label="cylindrical section001"
  Base = -> Cut233
  Tool = -> Cylinder414
FEATURE [Part::Box] Box001  label="Cube001"
  AttacherType = Attacher::AttachEngine3D
  Height = 10
  Length = 5
  Placement = pos=(20,-9,0) rot=(0,0,1;0rad)
  Width = 10
FEATURE [Part::Cylinder] Cylinder416
  Angle = 360
  AttacherType = Attacher::AttachEngine3D
  Height = 10
  Placement = pos=(25,-4,0) rot=(0,0,1;0rad)
  Radius = 2.5
FEATURE [Part::Cylinder] Cylinder417
  Angle = 360
  AttacherType = Attacher::AttachEngine3D
  Height = 10
  Placement = pos=(25,-4,0) rot=(0,0,1;0rad)
  Radius = 5
FEATURE [Part::MultiFuse] Fusion092
  Shapes = -> [Cylinder417,Box001]
FEATURE [Part::Cylinder] Cylinder418
  Angle = 360
  AttacherType = Attacher::AttachEngine3D
  Height = 63
  Radius = 21.5
FEATURE [Part::MultiFuse] Fusion093
  Shapes = -> [Cylinder418,Cylinder416]
FEATURE [Part::Cut] Cut236  label="Slider"
  Base = -> Fusion092
  Placement = pos=(0,0,22) rot=(0,0,1;0rad)
  Tool = -> Fusion093
FEATURE [Part::Cone] Cone010  label="Cone"
  Angle = 360
  AttacherType = Attacher::AttachEngine3D
  Height = 3.1
  Placement = pos=(0,0,123) rot=(0,0,1;0rad)
  Radius1 = 6
  Radius2 = 4.3
FEATURE [Part::MultiFuse] Fusion091  label="uitsparing001"
  Shapes = -> [Cylinder415,Cone010]
FEATURE [Part::Cut] Cut231  label="top001"
  Base = -> Common008
  Tool = -> Fusion091
FEATURE [Part::Compound] Compound204  label="Structure (external - 3 mm longer)"
  Links = -> [Cut235,Cut232,Cut231]
